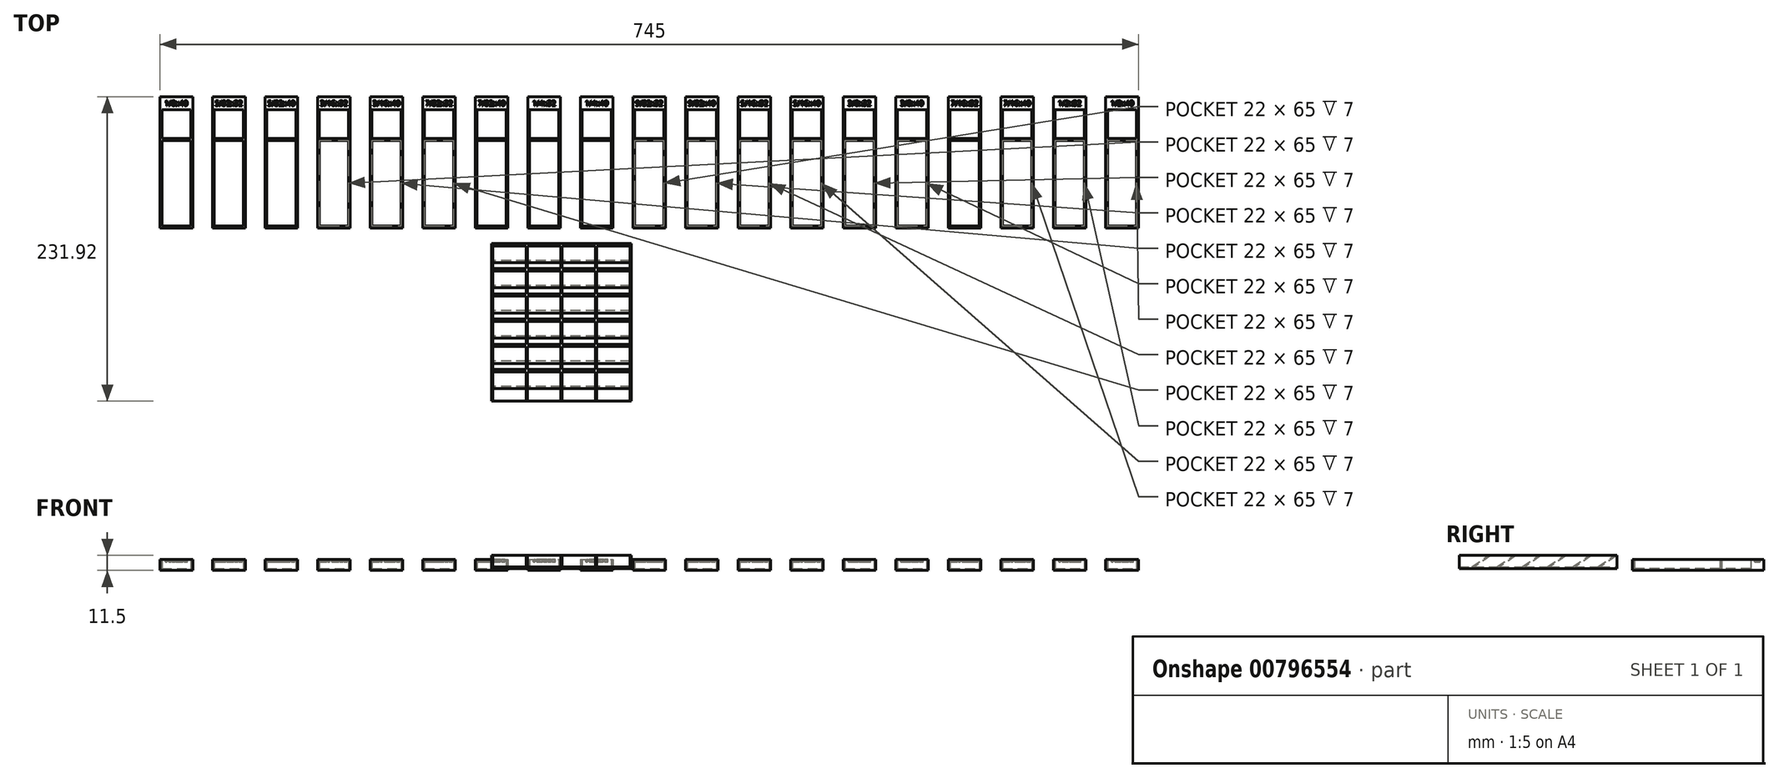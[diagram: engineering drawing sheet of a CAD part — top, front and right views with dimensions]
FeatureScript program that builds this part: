
annotation { "Feature Type Name" : "Feature", "Feature Type Description" : "" }
export const myFeature = defineFeature(function(context is Context, id is Id, definition is map)
    precondition{}
    {
        {
            var Q0;
            Q0=qCreatedBy(makeId("Top.planeOp"),FACE);
            var sketch = newSketch(context, id + "F0", { "sketchPlane" : qUnion([Q0])});
            skLineSegment(sketch, "E0.bottom", {"start": v(30.55, 66.22) * mm, "end": v(55.55, 66.22) * mm});
            skLineSegment(sketch, "E0.top", {"start": v(30.55, -33.78) * mm, "end": v(55.55, -33.78) * mm});
            skLineSegment(sketch, "E0.left", {"start": v(30.55, 66.22) * mm, "end": v(30.55, -33.78) * mm});
            skLineSegment(sketch, "E0.right", {"start": v(55.55, 66.22) * mm, "end": v(55.55, -33.78) * mm});
            skLineSegment(sketch, "E1.bottom", {"start": v(32.05, 56.22) * mm, "end": v(54.05, 56.22) * mm});
            skLineSegment(sketch, "E1.top", {"start": v(32.05, 34.22) * mm, "end": v(54.05, 34.22) * mm});
            skLineSegment(sketch, "E1.left", {"start": v(32.05, 56.22) * mm, "end": v(32.05, 34.22) * mm});
            skLineSegment(sketch, "E1.right", {"start": v(54.05, 56.22) * mm, "end": v(54.05, 34.22) * mm});
            skLineSegment(sketch, "E2.bottom", {"start": v(42.3, 32.72) * mm, "end": v(43.8, 32.72) * mm});
            skLineSegment(sketch, "E2.top", {"start": v(42.3, -32.28) * mm, "end": v(43.8, -32.28) * mm});
            skLineSegment(sketch, "E2.left", {"start": v(42.3, 32.72) * mm, "end": v(42.3, -32.28) * mm});
            skLineSegment(sketch, "E2.right", {"start": v(43.8, 32.72) * mm, "end": v(43.8, -32.28) * mm});
            skLineSegment(sketch, "E3.bottom", {"start": v(32.05, 32.72) * mm, "end": v(54.05, 32.72) * mm});
            skLineSegment(sketch, "E3.top", {"start": v(32.05, -32.28) * mm, "end": v(54.05, -32.28) * mm});
            skLineSegment(sketch, "E3.left", {"start": v(32.05, 32.72) * mm, "end": v(32.05, -32.28) * mm});
            skLineSegment(sketch, "E3.right", {"start": v(54.05, 32.72) * mm, "end": v(54.05, -32.28) * mm});
            skLineSegment(sketch, "E4", {"start": v(43.05, 66.22) * mm, "end": v(43.05, -33.78) * mm, "construction": true});
            skLineSegment(sketch, "E5.1.0.0", {"start": v(72.05, 34.22) * mm, "end": v(94.05, 34.22) * mm});
            skLineSegment(sketch, "E5.1.0.1", {"start": v(72.05, 56.22) * mm, "end": v(72.05, 34.22) * mm});
            skLineSegment(sketch, "E5.1.0.2", {"start": v(72.05, 32.72) * mm, "end": v(72.05, -32.28) * mm});
            skLineSegment(sketch, "E5.1.0.3", {"start": v(70.55, 66.22) * mm, "end": v(70.55, -33.78) * mm});
            skLineSegment(sketch, "E5.1.0.4", {"start": v(72.05, -32.28) * mm, "end": v(94.05, -32.28) * mm});
            skLineSegment(sketch, "E5.1.0.5", {"start": v(94.05, 32.72) * mm, "end": v(94.05, -32.28) * mm});
            skLineSegment(sketch, "E5.1.0.6", {"start": v(82.3, 32.72) * mm, "end": v(82.3, -32.28) * mm});
            skLineSegment(sketch, "E5.1.0.7", {"start": v(95.55, 66.22) * mm, "end": v(95.55, -33.78) * mm});
            skLineSegment(sketch, "E5.1.0.8", {"start": v(94.05, 56.22) * mm, "end": v(94.05, 34.22) * mm});
            skLineSegment(sketch, "E5.1.0.9", {"start": v(83.05, 66.22) * mm, "end": v(83.05, -33.78) * mm, "construction": true});
            skLineSegment(sketch, "E5.1.0.10", {"start": v(72.05, 32.72) * mm, "end": v(94.05, 32.72) * mm});
            skLineSegment(sketch, "E5.1.0.11", {"start": v(70.55, 66.22) * mm, "end": v(95.55, 66.22) * mm});
            skLineSegment(sketch, "E5.1.0.12", {"start": v(70.55, -33.78) * mm, "end": v(95.55, -33.78) * mm});
            skLineSegment(sketch, "E5.1.0.13", {"start": v(72.05, 56.22) * mm, "end": v(94.05, 56.22) * mm});
            skLineSegment(sketch, "E5.1.0.14", {"start": v(83.8, 32.72) * mm, "end": v(83.8, -32.28) * mm});
            skLineSegment(sketch, "E5.1.0.15", {"start": v(82.3, -32.28) * mm, "end": v(83.8, -32.28) * mm});
            skLineSegment(sketch, "E5.1.0.16", {"start": v(82.3, 32.72) * mm, "end": v(83.8, 32.72) * mm});
            skLineSegment(sketch, "E5.2.0.0", {"start": v(112.05, 34.22) * mm, "end": v(134.05, 34.22) * mm});
            skLineSegment(sketch, "E5.2.0.1", {"start": v(112.05, 56.22) * mm, "end": v(112.05, 34.22) * mm});
            skLineSegment(sketch, "E5.2.0.2", {"start": v(112.05, 32.72) * mm, "end": v(112.05, -32.28) * mm});
            skLineSegment(sketch, "E5.2.0.3", {"start": v(110.55, 66.22) * mm, "end": v(110.55, -33.78) * mm});
            skLineSegment(sketch, "E5.2.0.4", {"start": v(112.05, -32.28) * mm, "end": v(134.05, -32.28) * mm});
            skLineSegment(sketch, "E5.2.0.5", {"start": v(134.05, 32.72) * mm, "end": v(134.05, -32.28) * mm});
            skLineSegment(sketch, "E5.2.0.6", {"start": v(122.3, 32.72) * mm, "end": v(122.3, -32.28) * mm});
            skLineSegment(sketch, "E5.2.0.7", {"start": v(135.55, 66.22) * mm, "end": v(135.55, -33.78) * mm});
            skLineSegment(sketch, "E5.2.0.8", {"start": v(134.05, 56.22) * mm, "end": v(134.05, 34.22) * mm});
            skLineSegment(sketch, "E5.2.0.9", {"start": v(123.05, 66.22) * mm, "end": v(123.05, -33.78) * mm, "construction": true});
            skLineSegment(sketch, "E5.2.0.10", {"start": v(112.05, 32.72) * mm, "end": v(134.05, 32.72) * mm});
            skLineSegment(sketch, "E5.2.0.11", {"start": v(110.55, 66.22) * mm, "end": v(135.55, 66.22) * mm});
            skLineSegment(sketch, "E5.2.0.12", {"start": v(110.55, -33.78) * mm, "end": v(135.55, -33.78) * mm});
            skLineSegment(sketch, "E5.2.0.13", {"start": v(112.05, 56.22) * mm, "end": v(134.05, 56.22) * mm});
            skLineSegment(sketch, "E5.2.0.14", {"start": v(123.8, 32.72) * mm, "end": v(123.8, -32.28) * mm});
            skLineSegment(sketch, "E5.2.0.15", {"start": v(122.3, -32.28) * mm, "end": v(123.8, -32.28) * mm});
            skLineSegment(sketch, "E5.2.0.16", {"start": v(122.3, 32.72) * mm, "end": v(123.8, 32.72) * mm});
            skLineSegment(sketch, "E5.direction1", {"start": v(30.55, -33.78) * mm, "end": v(70.55, -33.78) * mm, "construction": true});
            skLineSegment(sketch, "E6.0.3.0", {"start": v(152.05, 34.22) * mm, "end": v(174.05, 34.22) * mm});
            skLineSegment(sketch, "E6.3.3.0", {"start": v(152.05, 56.22) * mm, "end": v(152.05, 34.22) * mm});
            skLineSegment(sketch, "E6.6.3.0", {"start": v(152.05, 32.72) * mm, "end": v(152.05, -32.28) * mm});
            skLineSegment(sketch, "E6.9.3.0", {"start": v(150.55, 66.22) * mm, "end": v(150.55, -33.78) * mm});
            skLineSegment(sketch, "E6.12.3.0", {"start": v(152.05, -32.28) * mm, "end": v(174.05, -32.28) * mm});
            skLineSegment(sketch, "E6.15.3.0", {"start": v(174.05, 32.72) * mm, "end": v(174.05, -32.28) * mm});
            skLineSegment(sketch, "E6.18.3.0", {"start": v(162.3, 32.72) * mm, "end": v(162.3, -32.28) * mm});
            skLineSegment(sketch, "E6.21.3.0", {"start": v(175.55, 66.22) * mm, "end": v(175.55, -33.78) * mm});
            skLineSegment(sketch, "E6.24.3.0", {"start": v(174.05, 56.22) * mm, "end": v(174.05, 34.22) * mm});
            skLineSegment(sketch, "E6.27.3.0", {"start": v(163.05, 66.22) * mm, "end": v(163.05, -33.78) * mm, "construction": true});
            skLineSegment(sketch, "E6.30.3.0", {"start": v(152.05, 32.72) * mm, "end": v(174.05, 32.72) * mm});
            skLineSegment(sketch, "E6.33.3.0", {"start": v(150.55, 66.22) * mm, "end": v(175.55, 66.22) * mm});
            skLineSegment(sketch, "E6.36.3.0", {"start": v(150.55, -33.78) * mm, "end": v(175.55, -33.78) * mm});
            skLineSegment(sketch, "E6.39.3.0", {"start": v(152.05, 56.22) * mm, "end": v(174.05, 56.22) * mm});
            skLineSegment(sketch, "E6.42.3.0", {"start": v(163.8, 32.72) * mm, "end": v(163.8, -32.28) * mm});
            skLineSegment(sketch, "E6.45.3.0", {"start": v(162.3, -32.28) * mm, "end": v(163.8, -32.28) * mm});
            skLineSegment(sketch, "E6.48.3.0", {"start": v(162.3, 32.72) * mm, "end": v(163.8, 32.72) * mm});
            skLineSegment(sketch, "E6.0.4.0", {"start": v(192.05, 34.22) * mm, "end": v(214.05, 34.22) * mm});
            skLineSegment(sketch, "E6.3.4.0", {"start": v(192.05, 56.22) * mm, "end": v(192.05, 34.22) * mm});
            skLineSegment(sketch, "E6.6.4.0", {"start": v(192.05, 32.72) * mm, "end": v(192.05, -32.28) * mm});
            skLineSegment(sketch, "E6.9.4.0", {"start": v(190.55, 66.22) * mm, "end": v(190.55, -33.78) * mm});
            skLineSegment(sketch, "E6.12.4.0", {"start": v(192.05, -32.28) * mm, "end": v(214.05, -32.28) * mm});
            skLineSegment(sketch, "E6.15.4.0", {"start": v(214.05, 32.72) * mm, "end": v(214.05, -32.28) * mm});
            skLineSegment(sketch, "E6.18.4.0", {"start": v(202.3, 32.72) * mm, "end": v(202.3, -32.28) * mm});
            skLineSegment(sketch, "E6.21.4.0", {"start": v(215.55, 66.22) * mm, "end": v(215.55, -33.78) * mm});
            skLineSegment(sketch, "E6.24.4.0", {"start": v(214.05, 56.22) * mm, "end": v(214.05, 34.22) * mm});
            skLineSegment(sketch, "E6.27.4.0", {"start": v(203.05, 66.22) * mm, "end": v(203.05, -33.78) * mm, "construction": true});
            skLineSegment(sketch, "E6.30.4.0", {"start": v(192.05, 32.72) * mm, "end": v(214.05, 32.72) * mm});
            skLineSegment(sketch, "E6.33.4.0", {"start": v(190.55, 66.22) * mm, "end": v(215.55, 66.22) * mm});
            skLineSegment(sketch, "E6.36.4.0", {"start": v(190.55, -33.78) * mm, "end": v(215.55, -33.78) * mm});
            skLineSegment(sketch, "E6.39.4.0", {"start": v(192.05, 56.22) * mm, "end": v(214.05, 56.22) * mm});
            skLineSegment(sketch, "E6.42.4.0", {"start": v(203.8, 32.72) * mm, "end": v(203.8, -32.28) * mm});
            skLineSegment(sketch, "E6.45.4.0", {"start": v(202.3, -32.28) * mm, "end": v(203.8, -32.28) * mm});
            skLineSegment(sketch, "E6.48.4.0", {"start": v(202.3, 32.72) * mm, "end": v(203.8, 32.72) * mm});
            skLineSegment(sketch, "E6.0.5.0", {"start": v(232.05, 34.22) * mm, "end": v(254.05, 34.22) * mm});
            skLineSegment(sketch, "E6.3.5.0", {"start": v(232.05, 56.22) * mm, "end": v(232.05, 34.22) * mm});
            skLineSegment(sketch, "E6.6.5.0", {"start": v(232.05, 32.72) * mm, "end": v(232.05, -32.28) * mm});
            skLineSegment(sketch, "E6.9.5.0", {"start": v(230.55, 66.22) * mm, "end": v(230.55, -33.78) * mm});
            skLineSegment(sketch, "E6.12.5.0", {"start": v(232.05, -32.28) * mm, "end": v(254.05, -32.28) * mm});
            skLineSegment(sketch, "E6.15.5.0", {"start": v(254.05, 32.72) * mm, "end": v(254.05, -32.28) * mm});
            skLineSegment(sketch, "E6.18.5.0", {"start": v(242.3, 32.72) * mm, "end": v(242.3, -32.28) * mm});
            skLineSegment(sketch, "E6.21.5.0", {"start": v(255.55, 66.22) * mm, "end": v(255.55, -33.78) * mm});
            skLineSegment(sketch, "E6.24.5.0", {"start": v(254.05, 56.22) * mm, "end": v(254.05, 34.22) * mm});
            skLineSegment(sketch, "E6.27.5.0", {"start": v(243.05, 66.22) * mm, "end": v(243.05, -33.78) * mm, "construction": true});
            skLineSegment(sketch, "E6.30.5.0", {"start": v(232.05, 32.72) * mm, "end": v(254.05, 32.72) * mm});
            skLineSegment(sketch, "E6.33.5.0", {"start": v(230.55, 66.22) * mm, "end": v(255.55, 66.22) * mm});
            skLineSegment(sketch, "E6.36.5.0", {"start": v(230.55, -33.78) * mm, "end": v(255.55, -33.78) * mm});
            skLineSegment(sketch, "E6.39.5.0", {"start": v(232.05, 56.22) * mm, "end": v(254.05, 56.22) * mm});
            skLineSegment(sketch, "E6.42.5.0", {"start": v(243.8, 32.72) * mm, "end": v(243.8, -32.28) * mm});
            skLineSegment(sketch, "E6.45.5.0", {"start": v(242.3, -32.28) * mm, "end": v(243.8, -32.28) * mm});
            skLineSegment(sketch, "E6.48.5.0", {"start": v(242.3, 32.72) * mm, "end": v(243.8, 32.72) * mm});
            skLineSegment(sketch, "E6.0.6.0", {"start": v(272.05, 34.22) * mm, "end": v(294.05, 34.22) * mm});
            skLineSegment(sketch, "E6.3.6.0", {"start": v(272.05, 56.22) * mm, "end": v(272.05, 34.22) * mm});
            skLineSegment(sketch, "E6.6.6.0", {"start": v(272.05, 32.72) * mm, "end": v(272.05, -32.28) * mm});
            skLineSegment(sketch, "E6.9.6.0", {"start": v(270.55, 66.22) * mm, "end": v(270.55, -33.78) * mm});
            skLineSegment(sketch, "E6.12.6.0", {"start": v(272.05, -32.28) * mm, "end": v(294.05, -32.28) * mm});
            skLineSegment(sketch, "E6.15.6.0", {"start": v(294.05, 32.72) * mm, "end": v(294.05, -32.28) * mm});
            skLineSegment(sketch, "E6.18.6.0", {"start": v(282.3, 32.72) * mm, "end": v(282.3, -32.28) * mm});
            skLineSegment(sketch, "E6.21.6.0", {"start": v(295.55, 66.22) * mm, "end": v(295.55, -33.78) * mm});
            skLineSegment(sketch, "E6.24.6.0", {"start": v(294.05, 56.22) * mm, "end": v(294.05, 34.22) * mm});
            skLineSegment(sketch, "E6.27.6.0", {"start": v(283.05, 66.22) * mm, "end": v(283.05, -33.78) * mm, "construction": true});
            skLineSegment(sketch, "E6.30.6.0", {"start": v(272.05, 32.72) * mm, "end": v(294.05, 32.72) * mm});
            skLineSegment(sketch, "E6.33.6.0", {"start": v(270.55, 66.22) * mm, "end": v(295.55, 66.22) * mm});
            skLineSegment(sketch, "E6.36.6.0", {"start": v(270.55, -33.78) * mm, "end": v(295.55, -33.78) * mm});
            skLineSegment(sketch, "E6.39.6.0", {"start": v(272.05, 56.22) * mm, "end": v(294.05, 56.22) * mm});
            skLineSegment(sketch, "E6.42.6.0", {"start": v(283.8, 32.72) * mm, "end": v(283.8, -32.28) * mm});
            skLineSegment(sketch, "E6.45.6.0", {"start": v(282.3, -32.28) * mm, "end": v(283.8, -32.28) * mm});
            skLineSegment(sketch, "E6.48.6.0", {"start": v(282.3, 32.72) * mm, "end": v(283.8, 32.72) * mm});
            skLineSegment(sketch, "E6.0.7.0", {"start": v(312.05, 34.22) * mm, "end": v(334.05, 34.22) * mm});
            skLineSegment(sketch, "E6.3.7.0", {"start": v(312.05, 56.22) * mm, "end": v(312.05, 34.22) * mm});
            skLineSegment(sketch, "E6.6.7.0", {"start": v(312.05, 32.72) * mm, "end": v(312.05, -32.28) * mm});
            skLineSegment(sketch, "E6.9.7.0", {"start": v(310.55, 66.22) * mm, "end": v(310.55, -33.78) * mm});
            skLineSegment(sketch, "E6.12.7.0", {"start": v(312.05, -32.28) * mm, "end": v(334.05, -32.28) * mm});
            skLineSegment(sketch, "E6.15.7.0", {"start": v(334.05, 32.72) * mm, "end": v(334.05, -32.28) * mm});
            skLineSegment(sketch, "E6.18.7.0", {"start": v(322.3, 32.72) * mm, "end": v(322.3, -32.28) * mm});
            skLineSegment(sketch, "E6.21.7.0", {"start": v(335.55, 66.22) * mm, "end": v(335.55, -33.78) * mm});
            skLineSegment(sketch, "E6.24.7.0", {"start": v(334.05, 56.22) * mm, "end": v(334.05, 34.22) * mm});
            skLineSegment(sketch, "E6.27.7.0", {"start": v(323.05, 66.22) * mm, "end": v(323.05, -33.78) * mm, "construction": true});
            skLineSegment(sketch, "E6.30.7.0", {"start": v(312.05, 32.72) * mm, "end": v(334.05, 32.72) * mm});
            skLineSegment(sketch, "E6.33.7.0", {"start": v(310.55, 66.22) * mm, "end": v(335.55, 66.22) * mm});
            skLineSegment(sketch, "E6.36.7.0", {"start": v(310.55, -33.78) * mm, "end": v(335.55, -33.78) * mm});
            skLineSegment(sketch, "E6.39.7.0", {"start": v(312.05, 56.22) * mm, "end": v(334.05, 56.22) * mm});
            skLineSegment(sketch, "E6.42.7.0", {"start": v(323.8, 32.72) * mm, "end": v(323.8, -32.28) * mm});
            skLineSegment(sketch, "E6.45.7.0", {"start": v(322.3, -32.28) * mm, "end": v(323.8, -32.28) * mm});
            skLineSegment(sketch, "E6.48.7.0", {"start": v(322.3, 32.72) * mm, "end": v(323.8, 32.72) * mm});
            skLineSegment(sketch, "E6.0.8.0", {"start": v(352.05, 34.22) * mm, "end": v(374.05, 34.22) * mm});
            skLineSegment(sketch, "E6.3.8.0", {"start": v(352.05, 56.22) * mm, "end": v(352.05, 34.22) * mm});
            skLineSegment(sketch, "E6.6.8.0", {"start": v(352.05, 32.72) * mm, "end": v(352.05, -32.28) * mm});
            skLineSegment(sketch, "E6.9.8.0", {"start": v(350.55, 66.22) * mm, "end": v(350.55, -33.78) * mm});
            skLineSegment(sketch, "E6.12.8.0", {"start": v(352.05, -32.28) * mm, "end": v(374.05, -32.28) * mm});
            skLineSegment(sketch, "E6.15.8.0", {"start": v(374.05, 32.72) * mm, "end": v(374.05, -32.28) * mm});
            skLineSegment(sketch, "E6.18.8.0", {"start": v(362.3, 32.72) * mm, "end": v(362.3, -32.28) * mm});
            skLineSegment(sketch, "E6.21.8.0", {"start": v(375.55, 66.22) * mm, "end": v(375.55, -33.78) * mm});
            skLineSegment(sketch, "E6.24.8.0", {"start": v(374.05, 56.22) * mm, "end": v(374.05, 34.22) * mm});
            skLineSegment(sketch, "E6.27.8.0", {"start": v(363.05, 66.22) * mm, "end": v(363.05, -33.78) * mm, "construction": true});
            skLineSegment(sketch, "E6.30.8.0", {"start": v(352.05, 32.72) * mm, "end": v(374.05, 32.72) * mm});
            skLineSegment(sketch, "E6.33.8.0", {"start": v(350.55, 66.22) * mm, "end": v(375.55, 66.22) * mm});
            skLineSegment(sketch, "E6.36.8.0", {"start": v(350.55, -33.78) * mm, "end": v(375.55, -33.78) * mm});
            skLineSegment(sketch, "E6.39.8.0", {"start": v(352.05, 56.22) * mm, "end": v(374.05, 56.22) * mm});
            skLineSegment(sketch, "E6.42.8.0", {"start": v(363.8, 32.72) * mm, "end": v(363.8, -32.28) * mm});
            skLineSegment(sketch, "E6.45.8.0", {"start": v(362.3, -32.28) * mm, "end": v(363.8, -32.28) * mm});
            skLineSegment(sketch, "E6.48.8.0", {"start": v(362.3, 32.72) * mm, "end": v(363.8, 32.72) * mm});
            skLineSegment(sketch, "E6.0.9.0", {"start": v(392.05, 34.22) * mm, "end": v(414.05, 34.22) * mm});
            skLineSegment(sketch, "E6.3.9.0", {"start": v(392.05, 56.22) * mm, "end": v(392.05, 34.22) * mm});
            skLineSegment(sketch, "E6.6.9.0", {"start": v(392.05, 32.72) * mm, "end": v(392.05, -32.28) * mm});
            skLineSegment(sketch, "E6.9.9.0", {"start": v(390.55, 66.22) * mm, "end": v(390.55, -33.78) * mm});
            skLineSegment(sketch, "E6.12.9.0", {"start": v(392.05, -32.28) * mm, "end": v(414.05, -32.28) * mm});
            skLineSegment(sketch, "E6.15.9.0", {"start": v(414.05, 32.72) * mm, "end": v(414.05, -32.28) * mm});
            skLineSegment(sketch, "E6.18.9.0", {"start": v(402.3, 32.72) * mm, "end": v(402.3, -32.28) * mm});
            skLineSegment(sketch, "E6.21.9.0", {"start": v(415.55, 66.22) * mm, "end": v(415.55, -33.78) * mm});
            skLineSegment(sketch, "E6.24.9.0", {"start": v(414.05, 56.22) * mm, "end": v(414.05, 34.22) * mm});
            skLineSegment(sketch, "E6.27.9.0", {"start": v(403.05, 66.22) * mm, "end": v(403.05, -33.78) * mm, "construction": true});
            skLineSegment(sketch, "E6.30.9.0", {"start": v(392.05, 32.72) * mm, "end": v(414.05, 32.72) * mm});
            skLineSegment(sketch, "E6.33.9.0", {"start": v(390.55, 66.22) * mm, "end": v(415.55, 66.22) * mm});
            skLineSegment(sketch, "E6.36.9.0", {"start": v(390.55, -33.78) * mm, "end": v(415.55, -33.78) * mm});
            skLineSegment(sketch, "E6.39.9.0", {"start": v(392.05, 56.22) * mm, "end": v(414.05, 56.22) * mm});
            skLineSegment(sketch, "E6.42.9.0", {"start": v(403.8, 32.72) * mm, "end": v(403.8, -32.28) * mm});
            skLineSegment(sketch, "E6.45.9.0", {"start": v(402.3, -32.28) * mm, "end": v(403.8, -32.28) * mm});
            skLineSegment(sketch, "E6.48.9.0", {"start": v(402.3, 32.72) * mm, "end": v(403.8, 32.72) * mm});
            skLineSegment(sketch, "E6.0.10.0", {"start": v(432.05, 34.22) * mm, "end": v(454.05, 34.22) * mm});
            skLineSegment(sketch, "E6.3.10.0", {"start": v(432.05, 56.22) * mm, "end": v(432.05, 34.22) * mm});
            skLineSegment(sketch, "E6.6.10.0", {"start": v(432.05, 32.72) * mm, "end": v(432.05, -32.28) * mm});
            skLineSegment(sketch, "E6.9.10.0", {"start": v(430.55, 66.22) * mm, "end": v(430.55, -33.78) * mm});
            skLineSegment(sketch, "E6.12.10.0", {"start": v(432.05, -32.28) * mm, "end": v(454.05, -32.28) * mm});
            skLineSegment(sketch, "E6.15.10.0", {"start": v(454.05, 32.72) * mm, "end": v(454.05, -32.28) * mm});
            skLineSegment(sketch, "E6.18.10.0", {"start": v(442.3, 32.72) * mm, "end": v(442.3, -32.28) * mm});
            skLineSegment(sketch, "E6.21.10.0", {"start": v(455.55, 66.22) * mm, "end": v(455.55, -33.78) * mm});
            skLineSegment(sketch, "E6.24.10.0", {"start": v(454.05, 56.22) * mm, "end": v(454.05, 34.22) * mm});
            skLineSegment(sketch, "E6.27.10.0", {"start": v(443.05, 66.22) * mm, "end": v(443.05, -33.78) * mm, "construction": true});
            skLineSegment(sketch, "E6.30.10.0", {"start": v(432.05, 32.72) * mm, "end": v(454.05, 32.72) * mm});
            skLineSegment(sketch, "E6.33.10.0", {"start": v(430.55, 66.22) * mm, "end": v(455.55, 66.22) * mm});
            skLineSegment(sketch, "E6.36.10.0", {"start": v(430.55, -33.78) * mm, "end": v(455.55, -33.78) * mm});
            skLineSegment(sketch, "E6.39.10.0", {"start": v(432.05, 56.22) * mm, "end": v(454.05, 56.22) * mm});
            skLineSegment(sketch, "E6.42.10.0", {"start": v(443.8, 32.72) * mm, "end": v(443.8, -32.28) * mm});
            skLineSegment(sketch, "E6.45.10.0", {"start": v(442.3, -32.28) * mm, "end": v(443.8, -32.28) * mm});
            skLineSegment(sketch, "E6.48.10.0", {"start": v(442.3, 32.72) * mm, "end": v(443.8, 32.72) * mm});
            skLineSegment(sketch, "E6.0.11.0", {"start": v(472.05, 34.22) * mm, "end": v(494.05, 34.22) * mm});
            skLineSegment(sketch, "E6.3.11.0", {"start": v(472.05, 56.22) * mm, "end": v(472.05, 34.22) * mm});
            skLineSegment(sketch, "E6.6.11.0", {"start": v(472.05, 32.72) * mm, "end": v(472.05, -32.28) * mm});
            skLineSegment(sketch, "E6.9.11.0", {"start": v(470.55, 66.22) * mm, "end": v(470.55, -33.78) * mm});
            skLineSegment(sketch, "E6.12.11.0", {"start": v(472.05, -32.28) * mm, "end": v(494.05, -32.28) * mm});
            skLineSegment(sketch, "E6.15.11.0", {"start": v(494.05, 32.72) * mm, "end": v(494.05, -32.28) * mm});
            skLineSegment(sketch, "E6.18.11.0", {"start": v(482.3, 32.72) * mm, "end": v(482.3, -32.28) * mm});
            skLineSegment(sketch, "E6.21.11.0", {"start": v(495.55, 66.22) * mm, "end": v(495.55, -33.78) * mm});
            skLineSegment(sketch, "E6.24.11.0", {"start": v(494.05, 56.22) * mm, "end": v(494.05, 34.22) * mm});
            skLineSegment(sketch, "E6.27.11.0", {"start": v(483.05, 66.22) * mm, "end": v(483.05, -33.78) * mm, "construction": true});
            skLineSegment(sketch, "E6.30.11.0", {"start": v(472.05, 32.72) * mm, "end": v(494.05, 32.72) * mm});
            skLineSegment(sketch, "E6.33.11.0", {"start": v(470.55, 66.22) * mm, "end": v(495.55, 66.22) * mm});
            skLineSegment(sketch, "E6.36.11.0", {"start": v(470.55, -33.78) * mm, "end": v(495.55, -33.78) * mm});
            skLineSegment(sketch, "E6.39.11.0", {"start": v(472.05, 56.22) * mm, "end": v(494.05, 56.22) * mm});
            skLineSegment(sketch, "E6.42.11.0", {"start": v(483.8, 32.72) * mm, "end": v(483.8, -32.28) * mm});
            skLineSegment(sketch, "E6.45.11.0", {"start": v(482.3, -32.28) * mm, "end": v(483.8, -32.28) * mm});
            skLineSegment(sketch, "E6.48.11.0", {"start": v(482.3, 32.72) * mm, "end": v(483.8, 32.72) * mm});
            skLineSegment(sketch, "E7.0.12.0", {"start": v(512.05, 34.22) * mm, "end": v(534.05, 34.22) * mm});
            skLineSegment(sketch, "E7.3.12.0", {"start": v(512.05, 56.22) * mm, "end": v(512.05, 34.22) * mm});
            skLineSegment(sketch, "E7.6.12.0", {"start": v(512.05, 32.72) * mm, "end": v(512.05, -32.28) * mm});
            skLineSegment(sketch, "E7.9.12.0", {"start": v(510.55, 66.22) * mm, "end": v(510.55, -33.78) * mm});
            skLineSegment(sketch, "E7.12.12.0", {"start": v(512.05, -32.28) * mm, "end": v(534.05, -32.28) * mm});
            skLineSegment(sketch, "E7.15.12.0", {"start": v(534.05, 32.72) * mm, "end": v(534.05, -32.28) * mm});
            skLineSegment(sketch, "E7.18.12.0", {"start": v(522.3, 32.72) * mm, "end": v(522.3, -32.28) * mm});
            skLineSegment(sketch, "E7.21.12.0", {"start": v(535.55, 66.22) * mm, "end": v(535.55, -33.78) * mm});
            skLineSegment(sketch, "E7.24.12.0", {"start": v(534.05, 56.22) * mm, "end": v(534.05, 34.22) * mm});
            skLineSegment(sketch, "E7.27.12.0", {"start": v(523.05, 66.22) * mm, "end": v(523.05, -33.78) * mm, "construction": true});
            skLineSegment(sketch, "E7.30.12.0", {"start": v(512.05, 32.72) * mm, "end": v(534.05, 32.72) * mm});
            skLineSegment(sketch, "E7.33.12.0", {"start": v(510.55, 66.22) * mm, "end": v(535.55, 66.22) * mm});
            skLineSegment(sketch, "E7.36.12.0", {"start": v(510.55, -33.78) * mm, "end": v(535.55, -33.78) * mm});
            skLineSegment(sketch, "E7.39.12.0", {"start": v(512.05, 56.22) * mm, "end": v(534.05, 56.22) * mm});
            skLineSegment(sketch, "E7.42.12.0", {"start": v(523.8, 32.72) * mm, "end": v(523.8, -32.28) * mm});
            skLineSegment(sketch, "E7.45.12.0", {"start": v(522.3, -32.28) * mm, "end": v(523.8, -32.28) * mm});
            skLineSegment(sketch, "E7.48.12.0", {"start": v(522.3, 32.72) * mm, "end": v(523.8, 32.72) * mm});
            skLineSegment(sketch, "E8.0.13.0", {"start": v(552.05, 34.22) * mm, "end": v(574.05, 34.22) * mm});
            skLineSegment(sketch, "E8.3.13.0", {"start": v(552.05, 56.22) * mm, "end": v(552.05, 34.22) * mm});
            skLineSegment(sketch, "E8.6.13.0", {"start": v(552.05, 32.72) * mm, "end": v(552.05, -32.28) * mm});
            skLineSegment(sketch, "E8.9.13.0", {"start": v(550.55, 66.22) * mm, "end": v(550.55, -33.78) * mm});
            skLineSegment(sketch, "E8.12.13.0", {"start": v(552.05, -32.28) * mm, "end": v(574.05, -32.28) * mm});
            skLineSegment(sketch, "E8.15.13.0", {"start": v(574.05, 32.72) * mm, "end": v(574.05, -32.28) * mm});
            skLineSegment(sketch, "E8.18.13.0", {"start": v(562.3, 32.72) * mm, "end": v(562.3, -32.28) * mm});
            skLineSegment(sketch, "E8.21.13.0", {"start": v(575.55, 66.22) * mm, "end": v(575.55, -33.78) * mm});
            skLineSegment(sketch, "E8.24.13.0", {"start": v(574.05, 56.22) * mm, "end": v(574.05, 34.22) * mm});
            skLineSegment(sketch, "E8.27.13.0", {"start": v(563.05, 66.22) * mm, "end": v(563.05, -33.78) * mm, "construction": true});
            skLineSegment(sketch, "E8.30.13.0", {"start": v(552.05, 32.72) * mm, "end": v(574.05, 32.72) * mm});
            skLineSegment(sketch, "E8.33.13.0", {"start": v(550.55, 66.22) * mm, "end": v(575.55, 66.22) * mm});
            skLineSegment(sketch, "E8.36.13.0", {"start": v(550.55, -33.78) * mm, "end": v(575.55, -33.78) * mm});
            skLineSegment(sketch, "E8.39.13.0", {"start": v(552.05, 56.22) * mm, "end": v(574.05, 56.22) * mm});
            skLineSegment(sketch, "E8.42.13.0", {"start": v(563.8, 32.72) * mm, "end": v(563.8, -32.28) * mm});
            skLineSegment(sketch, "E8.45.13.0", {"start": v(562.3, -32.28) * mm, "end": v(563.8, -32.28) * mm});
            skLineSegment(sketch, "E8.48.13.0", {"start": v(562.3, 32.72) * mm, "end": v(563.8, 32.72) * mm});
            skLineSegment(sketch, "E8.0.14.0", {"start": v(592.05, 34.22) * mm, "end": v(614.05, 34.22) * mm});
            skLineSegment(sketch, "E8.3.14.0", {"start": v(592.05, 56.22) * mm, "end": v(592.05, 34.22) * mm});
            skLineSegment(sketch, "E8.6.14.0", {"start": v(592.05, 32.72) * mm, "end": v(592.05, -32.28) * mm});
            skLineSegment(sketch, "E8.9.14.0", {"start": v(590.55, 66.22) * mm, "end": v(590.55, -33.78) * mm});
            skLineSegment(sketch, "E8.12.14.0", {"start": v(592.05, -32.28) * mm, "end": v(614.05, -32.28) * mm});
            skLineSegment(sketch, "E8.15.14.0", {"start": v(614.05, 32.72) * mm, "end": v(614.05, -32.28) * mm});
            skLineSegment(sketch, "E8.18.14.0", {"start": v(602.3, 32.72) * mm, "end": v(602.3, -32.28) * mm});
            skLineSegment(sketch, "E8.21.14.0", {"start": v(615.55, 66.22) * mm, "end": v(615.55, -33.78) * mm});
            skLineSegment(sketch, "E8.24.14.0", {"start": v(614.05, 56.22) * mm, "end": v(614.05, 34.22) * mm});
            skLineSegment(sketch, "E8.27.14.0", {"start": v(603.05, 66.22) * mm, "end": v(603.05, -33.78) * mm, "construction": true});
            skLineSegment(sketch, "E8.30.14.0", {"start": v(592.05, 32.72) * mm, "end": v(614.05, 32.72) * mm});
            skLineSegment(sketch, "E8.33.14.0", {"start": v(590.55, 66.22) * mm, "end": v(615.55, 66.22) * mm});
            skLineSegment(sketch, "E8.36.14.0", {"start": v(590.55, -33.78) * mm, "end": v(615.55, -33.78) * mm});
            skLineSegment(sketch, "E8.39.14.0", {"start": v(592.05, 56.22) * mm, "end": v(614.05, 56.22) * mm});
            skLineSegment(sketch, "E8.42.14.0", {"start": v(603.8, 32.72) * mm, "end": v(603.8, -32.28) * mm});
            skLineSegment(sketch, "E8.45.14.0", {"start": v(602.3, -32.28) * mm, "end": v(603.8, -32.28) * mm});
            skLineSegment(sketch, "E8.48.14.0", {"start": v(602.3, 32.72) * mm, "end": v(603.8, 32.72) * mm});
            skLineSegment(sketch, "E9.0.15.0", {"start": v(632.05, 34.22) * mm, "end": v(654.05, 34.22) * mm});
            skLineSegment(sketch, "E9.3.15.0", {"start": v(632.05, 56.22) * mm, "end": v(632.05, 34.22) * mm});
            skLineSegment(sketch, "E9.6.15.0", {"start": v(632.05, 32.72) * mm, "end": v(632.05, -32.28) * mm});
            skLineSegment(sketch, "E9.9.15.0", {"start": v(630.55, 66.22) * mm, "end": v(630.55, -33.78) * mm});
            skLineSegment(sketch, "E9.12.15.0", {"start": v(632.05, -32.28) * mm, "end": v(654.05, -32.28) * mm});
            skLineSegment(sketch, "E9.15.15.0", {"start": v(654.05, 32.72) * mm, "end": v(654.05, -32.28) * mm});
            skLineSegment(sketch, "E9.18.15.0", {"start": v(642.3, 32.72) * mm, "end": v(642.3, -32.28) * mm});
            skLineSegment(sketch, "E9.21.15.0", {"start": v(655.55, 66.22) * mm, "end": v(655.55, -33.78) * mm});
            skLineSegment(sketch, "E9.24.15.0", {"start": v(654.05, 56.22) * mm, "end": v(654.05, 34.22) * mm});
            skLineSegment(sketch, "E9.27.15.0", {"start": v(643.05, 66.22) * mm, "end": v(643.05, -33.78) * mm, "construction": true});
            skLineSegment(sketch, "E9.30.15.0", {"start": v(632.05, 32.72) * mm, "end": v(654.05, 32.72) * mm});
            skLineSegment(sketch, "E9.33.15.0", {"start": v(630.55, 66.22) * mm, "end": v(655.55, 66.22) * mm});
            skLineSegment(sketch, "E9.36.15.0", {"start": v(630.55, -33.78) * mm, "end": v(655.55, -33.78) * mm});
            skLineSegment(sketch, "E9.39.15.0", {"start": v(632.05, 56.22) * mm, "end": v(654.05, 56.22) * mm});
            skLineSegment(sketch, "E9.42.15.0", {"start": v(643.8, 32.72) * mm, "end": v(643.8, -32.28) * mm});
            skLineSegment(sketch, "E9.45.15.0", {"start": v(642.3, -32.28) * mm, "end": v(643.8, -32.28) * mm});
            skLineSegment(sketch, "E9.48.15.0", {"start": v(642.3, 32.72) * mm, "end": v(643.8, 32.72) * mm});
            skLineSegment(sketch, "E9.0.16.0", {"start": v(672.05, 34.22) * mm, "end": v(694.05, 34.22) * mm});
            skLineSegment(sketch, "E9.3.16.0", {"start": v(672.05, 56.22) * mm, "end": v(672.05, 34.22) * mm});
            skLineSegment(sketch, "E9.6.16.0", {"start": v(672.05, 32.72) * mm, "end": v(672.05, -32.28) * mm});
            skLineSegment(sketch, "E9.9.16.0", {"start": v(670.55, 66.22) * mm, "end": v(670.55, -33.78) * mm});
            skLineSegment(sketch, "E9.12.16.0", {"start": v(672.05, -32.28) * mm, "end": v(694.05, -32.28) * mm});
            skLineSegment(sketch, "E9.15.16.0", {"start": v(694.05, 32.72) * mm, "end": v(694.05, -32.28) * mm});
            skLineSegment(sketch, "E9.18.16.0", {"start": v(682.3, 32.72) * mm, "end": v(682.3, -32.28) * mm});
            skLineSegment(sketch, "E9.21.16.0", {"start": v(695.55, 66.22) * mm, "end": v(695.55, -33.78) * mm});
            skLineSegment(sketch, "E9.24.16.0", {"start": v(694.05, 56.22) * mm, "end": v(694.05, 34.22) * mm});
            skLineSegment(sketch, "E9.27.16.0", {"start": v(683.05, 66.22) * mm, "end": v(683.05, -33.78) * mm, "construction": true});
            skLineSegment(sketch, "E9.30.16.0", {"start": v(672.05, 32.72) * mm, "end": v(694.05, 32.72) * mm});
            skLineSegment(sketch, "E9.33.16.0", {"start": v(670.55, 66.22) * mm, "end": v(695.55, 66.22) * mm});
            skLineSegment(sketch, "E9.36.16.0", {"start": v(670.55, -33.78) * mm, "end": v(695.55, -33.78) * mm});
            skLineSegment(sketch, "E9.39.16.0", {"start": v(672.05, 56.22) * mm, "end": v(694.05, 56.22) * mm});
            skLineSegment(sketch, "E9.42.16.0", {"start": v(683.8, 32.72) * mm, "end": v(683.8, -32.28) * mm});
            skLineSegment(sketch, "E9.45.16.0", {"start": v(682.3, -32.28) * mm, "end": v(683.8, -32.28) * mm});
            skLineSegment(sketch, "E9.48.16.0", {"start": v(682.3, 32.72) * mm, "end": v(683.8, 32.72) * mm});
            skLineSegment(sketch, "E9.0.17.0", {"start": v(712.05, 34.22) * mm, "end": v(734.05, 34.22) * mm});
            skLineSegment(sketch, "E9.3.17.0", {"start": v(712.05, 56.22) * mm, "end": v(712.05, 34.22) * mm});
            skLineSegment(sketch, "E9.6.17.0", {"start": v(712.05, 32.72) * mm, "end": v(712.05, -32.28) * mm});
            skLineSegment(sketch, "E9.9.17.0", {"start": v(710.55, 66.22) * mm, "end": v(710.55, -33.78) * mm});
            skLineSegment(sketch, "E9.12.17.0", {"start": v(712.05, -32.28) * mm, "end": v(734.05, -32.28) * mm});
            skLineSegment(sketch, "E9.15.17.0", {"start": v(734.05, 32.72) * mm, "end": v(734.05, -32.28) * mm});
            skLineSegment(sketch, "E9.18.17.0", {"start": v(722.3, 32.72) * mm, "end": v(722.3, -32.28) * mm});
            skLineSegment(sketch, "E9.21.17.0", {"start": v(735.55, 66.22) * mm, "end": v(735.55, -33.78) * mm});
            skLineSegment(sketch, "E9.24.17.0", {"start": v(734.05, 56.22) * mm, "end": v(734.05, 34.22) * mm});
            skLineSegment(sketch, "E9.27.17.0", {"start": v(723.05, 66.22) * mm, "end": v(723.05, -33.78) * mm, "construction": true});
            skLineSegment(sketch, "E9.30.17.0", {"start": v(712.05, 32.72) * mm, "end": v(734.05, 32.72) * mm});
            skLineSegment(sketch, "E9.33.17.0", {"start": v(710.55, 66.22) * mm, "end": v(735.55, 66.22) * mm});
            skLineSegment(sketch, "E9.36.17.0", {"start": v(710.55, -33.78) * mm, "end": v(735.55, -33.78) * mm});
            skLineSegment(sketch, "E9.39.17.0", {"start": v(712.05, 56.22) * mm, "end": v(734.05, 56.22) * mm});
            skLineSegment(sketch, "E9.42.17.0", {"start": v(723.8, 32.72) * mm, "end": v(723.8, -32.28) * mm});
            skLineSegment(sketch, "E9.45.17.0", {"start": v(722.3, -32.28) * mm, "end": v(723.8, -32.28) * mm});
            skLineSegment(sketch, "E9.48.17.0", {"start": v(722.3, 32.72) * mm, "end": v(723.8, 32.72) * mm});
            skLineSegment(sketch, "E9.0.18.0", {"start": v(752.05, 34.22) * mm, "end": v(774.05, 34.22) * mm});
            skLineSegment(sketch, "E9.3.18.0", {"start": v(752.05, 56.22) * mm, "end": v(752.05, 34.22) * mm});
            skLineSegment(sketch, "E9.6.18.0", {"start": v(752.05, 32.72) * mm, "end": v(752.05, -32.28) * mm});
            skLineSegment(sketch, "E9.9.18.0", {"start": v(750.55, 66.22) * mm, "end": v(750.55, -33.78) * mm});
            skLineSegment(sketch, "E9.12.18.0", {"start": v(752.05, -32.28) * mm, "end": v(774.05, -32.28) * mm});
            skLineSegment(sketch, "E9.15.18.0", {"start": v(774.05, 32.72) * mm, "end": v(774.05, -32.28) * mm});
            skLineSegment(sketch, "E9.18.18.0", {"start": v(762.3, 32.72) * mm, "end": v(762.3, -32.28) * mm});
            skLineSegment(sketch, "E9.21.18.0", {"start": v(775.55, 66.22) * mm, "end": v(775.55, -33.78) * mm});
            skLineSegment(sketch, "E9.24.18.0", {"start": v(774.05, 56.22) * mm, "end": v(774.05, 34.22) * mm});
            skLineSegment(sketch, "E9.27.18.0", {"start": v(763.05, 66.22) * mm, "end": v(763.05, -33.78) * mm, "construction": true});
            skLineSegment(sketch, "E9.30.18.0", {"start": v(752.05, 32.72) * mm, "end": v(774.05, 32.72) * mm});
            skLineSegment(sketch, "E9.33.18.0", {"start": v(750.55, 66.22) * mm, "end": v(775.55, 66.22) * mm});
            skLineSegment(sketch, "E9.36.18.0", {"start": v(750.55, -33.78) * mm, "end": v(775.55, -33.78) * mm});
            skLineSegment(sketch, "E9.39.18.0", {"start": v(752.05, 56.22) * mm, "end": v(774.05, 56.22) * mm});
            skLineSegment(sketch, "E9.42.18.0", {"start": v(763.8, 32.72) * mm, "end": v(763.8, -32.28) * mm});
            skLineSegment(sketch, "E9.45.18.0", {"start": v(762.3, -32.28) * mm, "end": v(763.8, -32.28) * mm});
            skLineSegment(sketch, "E9.48.18.0", {"start": v(762.3, 32.72) * mm, "end": v(763.8, 32.72) * mm});
            skSolve(sketch);
        }
        {
            var Q0;
            Q0=qCreatedBy(makeId("Top.planeOp"),FACE);
            var sketch = newSketch(context, id + "F1", { "sketchPlane" : qUnion([Q0])});
            skLineSegment(sketch, "E10.bottom", {"start": v(30.55, 66.22) * mm, "end": v(55.55, 66.22) * mm});
            skLineSegment(sketch, "E10.top", {"start": v(30.55, -33.78) * mm, "end": v(55.55, -33.78) * mm});
            skLineSegment(sketch, "E10.left", {"start": v(30.55, 66.22) * mm, "end": v(30.55, -33.78) * mm});
            skLineSegment(sketch, "E10.right", {"start": v(55.55, 66.22) * mm, "end": v(55.55, -33.78) * mm});
            skLineSegment(sketch, "E11.1.0.0", {"start": v(70.55, 66.22) * mm, "end": v(95.55, 66.22) * mm});
            skLineSegment(sketch, "E11.1.0.1", {"start": v(70.55, 66.22) * mm, "end": v(70.55, -33.78) * mm});
            skLineSegment(sketch, "E11.1.0.2", {"start": v(70.55, -33.78) * mm, "end": v(95.55, -33.78) * mm});
            skLineSegment(sketch, "E11.1.0.3", {"start": v(95.55, 66.22) * mm, "end": v(95.55, -33.78) * mm});
            skLineSegment(sketch, "E11.2.0.0", {"start": v(110.55, 66.22) * mm, "end": v(135.55, 66.22) * mm});
            skLineSegment(sketch, "E11.2.0.1", {"start": v(110.55, 66.22) * mm, "end": v(110.55, -33.78) * mm});
            skLineSegment(sketch, "E11.2.0.2", {"start": v(110.55, -33.78) * mm, "end": v(135.55, -33.78) * mm});
            skLineSegment(sketch, "E11.2.0.3", {"start": v(135.55, 66.22) * mm, "end": v(135.55, -33.78) * mm});
            skLineSegment(sketch, "E11.direction1", {"start": v(30.55, 66.22) * mm, "end": v(70.55, 66.22) * mm, "construction": true});
            skLineSegment(sketch, "E12.0.3.0", {"start": v(150.55, 66.22) * mm, "end": v(175.55, 66.22) * mm});
            skLineSegment(sketch, "E12.3.3.0", {"start": v(150.55, 66.22) * mm, "end": v(150.55, -33.78) * mm});
            skLineSegment(sketch, "E12.6.3.0", {"start": v(150.55, -33.78) * mm, "end": v(175.55, -33.78) * mm});
            skLineSegment(sketch, "E12.9.3.0", {"start": v(175.55, 66.22) * mm, "end": v(175.55, -33.78) * mm});
            skLineSegment(sketch, "E12.0.4.0", {"start": v(190.55, 66.22) * mm, "end": v(215.55, 66.22) * mm});
            skLineSegment(sketch, "E12.3.4.0", {"start": v(190.55, 66.22) * mm, "end": v(190.55, -33.78) * mm});
            skLineSegment(sketch, "E12.6.4.0", {"start": v(190.55, -33.78) * mm, "end": v(215.55, -33.78) * mm});
            skLineSegment(sketch, "E12.9.4.0", {"start": v(215.55, 66.22) * mm, "end": v(215.55, -33.78) * mm});
            skLineSegment(sketch, "E12.0.5.0", {"start": v(230.55, 66.22) * mm, "end": v(255.55, 66.22) * mm});
            skLineSegment(sketch, "E12.3.5.0", {"start": v(230.55, 66.22) * mm, "end": v(230.55, -33.78) * mm});
            skLineSegment(sketch, "E12.6.5.0", {"start": v(230.55, -33.78) * mm, "end": v(255.55, -33.78) * mm});
            skLineSegment(sketch, "E12.9.5.0", {"start": v(255.55, 66.22) * mm, "end": v(255.55, -33.78) * mm});
            skLineSegment(sketch, "E12.0.6.0", {"start": v(270.55, 66.22) * mm, "end": v(295.55, 66.22) * mm});
            skLineSegment(sketch, "E12.3.6.0", {"start": v(270.55, 66.22) * mm, "end": v(270.55, -33.78) * mm});
            skLineSegment(sketch, "E12.6.6.0", {"start": v(270.55, -33.78) * mm, "end": v(295.55, -33.78) * mm});
            skLineSegment(sketch, "E12.9.6.0", {"start": v(295.55, 66.22) * mm, "end": v(295.55, -33.78) * mm});
            skLineSegment(sketch, "E12.0.7.0", {"start": v(310.55, 66.22) * mm, "end": v(335.55, 66.22) * mm});
            skLineSegment(sketch, "E12.3.7.0", {"start": v(310.55, 66.22) * mm, "end": v(310.55, -33.78) * mm});
            skLineSegment(sketch, "E12.6.7.0", {"start": v(310.55, -33.78) * mm, "end": v(335.55, -33.78) * mm});
            skLineSegment(sketch, "E12.9.7.0", {"start": v(335.55, 66.22) * mm, "end": v(335.55, -33.78) * mm});
            skLineSegment(sketch, "E12.0.8.0", {"start": v(350.55, 66.22) * mm, "end": v(375.55, 66.22) * mm});
            skLineSegment(sketch, "E12.3.8.0", {"start": v(350.55, 66.22) * mm, "end": v(350.55, -33.78) * mm});
            skLineSegment(sketch, "E12.6.8.0", {"start": v(350.55, -33.78) * mm, "end": v(375.55, -33.78) * mm});
            skLineSegment(sketch, "E12.9.8.0", {"start": v(375.55, 66.22) * mm, "end": v(375.55, -33.78) * mm});
            skLineSegment(sketch, "E12.0.9.0", {"start": v(390.55, 66.22) * mm, "end": v(415.55, 66.22) * mm});
            skLineSegment(sketch, "E12.3.9.0", {"start": v(390.55, 66.22) * mm, "end": v(390.55, -33.78) * mm});
            skLineSegment(sketch, "E12.6.9.0", {"start": v(390.55, -33.78) * mm, "end": v(415.55, -33.78) * mm});
            skLineSegment(sketch, "E12.9.9.0", {"start": v(415.55, 66.22) * mm, "end": v(415.55, -33.78) * mm});
            skLineSegment(sketch, "E12.0.10.0", {"start": v(430.55, 66.22) * mm, "end": v(455.55, 66.22) * mm});
            skLineSegment(sketch, "E12.3.10.0", {"start": v(430.55, 66.22) * mm, "end": v(430.55, -33.78) * mm});
            skLineSegment(sketch, "E12.6.10.0", {"start": v(430.55, -33.78) * mm, "end": v(455.55, -33.78) * mm});
            skLineSegment(sketch, "E12.9.10.0", {"start": v(455.55, 66.22) * mm, "end": v(455.55, -33.78) * mm});
            skLineSegment(sketch, "E12.0.11.0", {"start": v(470.55, 66.22) * mm, "end": v(495.55, 66.22) * mm});
            skLineSegment(sketch, "E12.3.11.0", {"start": v(470.55, 66.22) * mm, "end": v(470.55, -33.78) * mm});
            skLineSegment(sketch, "E12.6.11.0", {"start": v(470.55, -33.78) * mm, "end": v(495.55, -33.78) * mm});
            skLineSegment(sketch, "E12.9.11.0", {"start": v(495.55, 66.22) * mm, "end": v(495.55, -33.78) * mm});
            skLineSegment(sketch, "E13.0.12.0", {"start": v(510.55, 66.22) * mm, "end": v(535.55, 66.22) * mm});
            skLineSegment(sketch, "E13.3.12.0", {"start": v(510.55, 66.22) * mm, "end": v(510.55, -33.78) * mm});
            skLineSegment(sketch, "E13.6.12.0", {"start": v(510.55, -33.78) * mm, "end": v(535.55, -33.78) * mm});
            skLineSegment(sketch, "E13.9.12.0", {"start": v(535.55, 66.22) * mm, "end": v(535.55, -33.78) * mm});
            skLineSegment(sketch, "E13.0.13.0", {"start": v(550.55, 66.22) * mm, "end": v(575.55, 66.22) * mm});
            skLineSegment(sketch, "E13.3.13.0", {"start": v(550.55, 66.22) * mm, "end": v(550.55, -33.78) * mm});
            skLineSegment(sketch, "E13.6.13.0", {"start": v(550.55, -33.78) * mm, "end": v(575.55, -33.78) * mm});
            skLineSegment(sketch, "E13.9.13.0", {"start": v(575.55, 66.22) * mm, "end": v(575.55, -33.78) * mm});
            skLineSegment(sketch, "E13.0.14.0", {"start": v(590.55, 66.22) * mm, "end": v(615.55, 66.22) * mm});
            skLineSegment(sketch, "E13.3.14.0", {"start": v(590.55, 66.22) * mm, "end": v(590.55, -33.78) * mm});
            skLineSegment(sketch, "E13.6.14.0", {"start": v(590.55, -33.78) * mm, "end": v(615.55, -33.78) * mm});
            skLineSegment(sketch, "E13.9.14.0", {"start": v(615.55, 66.22) * mm, "end": v(615.55, -33.78) * mm});
            skLineSegment(sketch, "E14.0.15.0", {"start": v(630.55, 66.22) * mm, "end": v(655.55, 66.22) * mm});
            skLineSegment(sketch, "E14.3.15.0", {"start": v(630.55, 66.22) * mm, "end": v(630.55, -33.78) * mm});
            skLineSegment(sketch, "E14.6.15.0", {"start": v(630.55, -33.78) * mm, "end": v(655.55, -33.78) * mm});
            skLineSegment(sketch, "E14.9.15.0", {"start": v(655.55, 66.22) * mm, "end": v(655.55, -33.78) * mm});
            skLineSegment(sketch, "E14.0.16.0", {"start": v(670.55, 66.22) * mm, "end": v(695.55, 66.22) * mm});
            skLineSegment(sketch, "E14.3.16.0", {"start": v(670.55, 66.22) * mm, "end": v(670.55, -33.78) * mm});
            skLineSegment(sketch, "E14.6.16.0", {"start": v(670.55, -33.78) * mm, "end": v(695.55, -33.78) * mm});
            skLineSegment(sketch, "E14.9.16.0", {"start": v(695.55, 66.22) * mm, "end": v(695.55, -33.78) * mm});
            skLineSegment(sketch, "E14.0.17.0", {"start": v(710.55, 66.22) * mm, "end": v(735.55, 66.22) * mm});
            skLineSegment(sketch, "E14.3.17.0", {"start": v(710.55, 66.22) * mm, "end": v(710.55, -33.78) * mm});
            skLineSegment(sketch, "E14.6.17.0", {"start": v(710.55, -33.78) * mm, "end": v(735.55, -33.78) * mm});
            skLineSegment(sketch, "E14.9.17.0", {"start": v(735.55, 66.22) * mm, "end": v(735.55, -33.78) * mm});
            skLineSegment(sketch, "E14.0.18.0", {"start": v(750.55, 66.22) * mm, "end": v(775.55, 66.22) * mm});
            skLineSegment(sketch, "E14.3.18.0", {"start": v(750.55, 66.22) * mm, "end": v(750.55, -33.78) * mm});
            skLineSegment(sketch, "E14.6.18.0", {"start": v(750.55, -33.78) * mm, "end": v(775.55, -33.78) * mm});
            skLineSegment(sketch, "E14.9.18.0", {"start": v(775.55, 66.22) * mm, "end": v(775.55, -33.78) * mm});
            skSolve(sketch);
        }
        {
            var Q0;
            {Q0=qUnion([makeQuery(id+"F0.imprint","IMPRINT",FACE,{"disambiguationData":[TD([[makeQuery(id+"F0.imprint","IMPRINT",EDGE,{"derivedFrom":sQuery(id+"F0.wireOp",EDGE,"E0.bottom")}),-1.0]])]}),makeQuery(id+"F0.imprint","IMPRINT",FACE,{"disambiguationData":[TD([[makeQuery(id+"F0.imprint","IMPRINT",EDGE,{"derivedFrom":sQuery(id+"F0.wireOp",EDGE,"E5.1.0.0")}),-1.0]])]}),makeQuery(id+"F0.imprint","IMPRINT",FACE,{"disambiguationData":[TD([[makeQuery(id+"F0.imprint","IMPRINT",EDGE,{"derivedFrom":sQuery(id+"F0.wireOp",EDGE,"E5.2.0.0")}),-1.0]])]}),makeQuery(id+"F0.imprint","IMPRINT",FACE,{"disambiguationData":[TD([[makeQuery(id+"F0.imprint","IMPRINT",EDGE,{"derivedFrom":sQuery(id+"F0.wireOp",EDGE,"E6.0.3.0")}),-1.0]])]}),makeQuery(id+"F0.imprint","IMPRINT",FACE,{"disambiguationData":[TD([[makeQuery(id+"F0.imprint","IMPRINT",EDGE,{"derivedFrom":sQuery(id+"F0.wireOp",EDGE,"E6.0.4.0")}),-1.0]])]}),makeQuery(id+"F0.imprint","IMPRINT",FACE,{"disambiguationData":[TD([[makeQuery(id+"F0.imprint","IMPRINT",EDGE,{"derivedFrom":sQuery(id+"F0.wireOp",EDGE,"E6.0.5.0")}),-1.0]])]}),makeQuery(id+"F0.imprint","IMPRINT",FACE,{"disambiguationData":[TD([[makeQuery(id+"F0.imprint","IMPRINT",EDGE,{"derivedFrom":sQuery(id+"F0.wireOp",EDGE,"E6.0.6.0")}),-1.0]])]}),makeQuery(id+"F0.imprint","IMPRINT",FACE,{"disambiguationData":[TD([[makeQuery(id+"F0.imprint","IMPRINT",EDGE,{"derivedFrom":sQuery(id+"F0.wireOp",EDGE,"E6.0.7.0")}),-1.0]])]}),makeQuery(id+"F0.imprint","IMPRINT",FACE,{"disambiguationData":[TD([[makeQuery(id+"F0.imprint","IMPRINT",EDGE,{"derivedFrom":sQuery(id+"F0.wireOp",EDGE,"E6.0.8.0")}),-1.0]])]}),makeQuery(id+"F0.imprint","IMPRINT",FACE,{"disambiguationData":[TD([[makeQuery(id+"F0.imprint","IMPRINT",EDGE,{"derivedFrom":sQuery(id+"F0.wireOp",EDGE,"E6.0.9.0")}),-1.0]])]}),makeQuery(id+"F0.imprint","IMPRINT",FACE,{"disambiguationData":[TD([[makeQuery(id+"F0.imprint","IMPRINT",EDGE,{"derivedFrom":sQuery(id+"F0.wireOp",EDGE,"E6.0.10.0")}),-1.0]])]}),makeQuery(id+"F0.imprint","IMPRINT",FACE,{"disambiguationData":[TD([[makeQuery(id+"F0.imprint","IMPRINT",EDGE,{"derivedFrom":sQuery(id+"F0.wireOp",EDGE,"E6.0.11.0")}),-1.0]])]}),makeQuery(id+"F0.imprint","IMPRINT",FACE,{"disambiguationData":[TD([[makeQuery(id+"F0.imprint","IMPRINT",EDGE,{"derivedFrom":sQuery(id+"F0.wireOp",EDGE,"E7.0.12.0")}),-1.0]])]}),makeQuery(id+"F0.imprint","IMPRINT",FACE,{"disambiguationData":[TD([[makeQuery(id+"F0.imprint","IMPRINT",EDGE,{"derivedFrom":sQuery(id+"F0.wireOp",EDGE,"E8.0.13.0")}),-1.0]])]}),makeQuery(id+"F0.imprint","IMPRINT",FACE,{"disambiguationData":[TD([[makeQuery(id+"F0.imprint","IMPRINT",EDGE,{"derivedFrom":sQuery(id+"F0.wireOp",EDGE,"E8.0.14.0")}),-1.0]])]}),makeQuery(id+"F0.imprint","IMPRINT",FACE,{"disambiguationData":[TD([[makeQuery(id+"F0.imprint","IMPRINT",EDGE,{"derivedFrom":sQuery(id+"F0.wireOp",EDGE,"E9.0.15.0")}),-1.0]])]}),makeQuery(id+"F0.imprint","IMPRINT",FACE,{"disambiguationData":[TD([[makeQuery(id+"F0.imprint","IMPRINT",EDGE,{"derivedFrom":sQuery(id+"F0.wireOp",EDGE,"E9.0.16.0")}),-1.0]])]}),makeQuery(id+"F0.imprint","IMPRINT",FACE,{"disambiguationData":[TD([[makeQuery(id+"F0.imprint","IMPRINT",EDGE,{"derivedFrom":sQuery(id+"F0.wireOp",EDGE,"E9.0.17.0")}),-1.0]])]}),makeQuery(id+"F0.imprint","IMPRINT",FACE,{"disambiguationData":[TD([[makeQuery(id+"F0.imprint","IMPRINT",EDGE,{"derivedFrom":sQuery(id+"F0.wireOp",EDGE,"E9.0.18.0")}),-1.0]])]})]);}
            extrude(context, id + "F2", {"entities" : qUnion([Q0]), "depth" : 7 * mm, "offsetDistance" : 25 * mm});
        }
        {
            var Q0;
            Q0=qSketchRegion(id+"F1",true);
            extrude(context, id + "F3", {"entities" : qUnion([Q0]), "operationType" : NewBodyOperationType.ADD, "oppositeDirection" : true, "depth" : 1.5 * mm, "offsetDistance" : 25 * mm});
        }
        {
            var Q0;
            Q0=makeQuery(id+"F2.opExtrude","CAP_FACE",FACE,{"disambiguationData":[OSD([sQuery(id+"F0.wireOp",EDGE,"E0.bottom"),sQuery(id+"F0.wireOp",EDGE,"E0.top"),sQuery(id+"F0.wireOp",EDGE,"E0.left"),sQuery(id+"F0.wireOp",EDGE,"E0.right"),sQuery(id+"F0.wireOp",EDGE,"E1.bottom"),sQuery(id+"F0.wireOp",EDGE,"E1.top"),sQuery(id+"F0.wireOp",EDGE,"E1.left"),sQuery(id+"F0.wireOp",EDGE,"E1.right"),sQuery(id+"F0.wireOp",EDGE,"E2.bottom"),sQuery(id+"F0.wireOp",EDGE,"E2.top"),sQuery(id+"F0.wireOp",EDGE,"E3.bottom"),sQuery(id+"F0.wireOp",EDGE,"E3.top"),sQuery(id+"F0.wireOp",EDGE,"E3.left"),sQuery(id+"F0.wireOp",EDGE,"E3.right")])],"isStart":false});
            var sketch = newSketch(context, id + "F4", { "sketchPlane" : qUnion([Q0])});
            skText(sketch, "E15", { "text": "1/8x40", "fontName": "OpenSans-Regular.ttf"});
            const initialGuessF4  = {"E15": [0.03418, 0.05922, 1, 0, 0.004]};
            skSetInitialGuess(sketch, initialGuessF4);
            skSolve(sketch);
        }
        {
            var Q0;
            Q0=makeQuery(id+"F2.opExtrude","CAP_FACE",FACE,{"disambiguationData":[OSD([sQuery(id+"F0.wireOp",EDGE,"E5.1.0.0"),sQuery(id+"F0.wireOp",EDGE,"E5.1.0.1"),sQuery(id+"F0.wireOp",EDGE,"E5.1.0.2"),sQuery(id+"F0.wireOp",EDGE,"E5.1.0.3"),sQuery(id+"F0.wireOp",EDGE,"E5.1.0.4"),sQuery(id+"F0.wireOp",EDGE,"E5.1.0.5"),sQuery(id+"F0.wireOp",EDGE,"E5.1.0.7"),sQuery(id+"F0.wireOp",EDGE,"E5.1.0.8"),sQuery(id+"F0.wireOp",EDGE,"E5.1.0.10"),sQuery(id+"F0.wireOp",EDGE,"E5.1.0.11"),sQuery(id+"F0.wireOp",EDGE,"E5.1.0.12"),sQuery(id+"F0.wireOp",EDGE,"E5.1.0.13")])],"isStart":false});
            var sketch = newSketch(context, id + "F5", { "sketchPlane" : qUnion([Q0])});
            skText(sketch, "E16", { "text": "5/32x32", "fontName": "OpenSans-Regular.ttf"});
            const initialGuessF5  = {"E16": [0.0726, 0.05922, 1, 0, 0.004]};
            skSetInitialGuess(sketch, initialGuessF5);
            skSolve(sketch);
        }
        {
            var Q0;
            Q0=makeQuery(id+"F2.opExtrude","CAP_FACE",FACE,{"disambiguationData":[OSD([sQuery(id+"F0.wireOp",EDGE,"E5.2.0.0"),sQuery(id+"F0.wireOp",EDGE,"E5.2.0.1"),sQuery(id+"F0.wireOp",EDGE,"E5.2.0.2"),sQuery(id+"F0.wireOp",EDGE,"E5.2.0.3"),sQuery(id+"F0.wireOp",EDGE,"E5.2.0.4"),sQuery(id+"F0.wireOp",EDGE,"E5.2.0.5"),sQuery(id+"F0.wireOp",EDGE,"E5.2.0.7"),sQuery(id+"F0.wireOp",EDGE,"E5.2.0.8"),sQuery(id+"F0.wireOp",EDGE,"E5.2.0.10"),sQuery(id+"F0.wireOp",EDGE,"E5.2.0.11"),sQuery(id+"F0.wireOp",EDGE,"E5.2.0.12"),sQuery(id+"F0.wireOp",EDGE,"E5.2.0.13")])],"isStart":false});
            var sketch = newSketch(context, id + "F6", { "sketchPlane" : qUnion([Q0])});
            skText(sketch, "E17", { "text": "5/32x40", "fontName": "OpenSans-Regular.ttf"});
            const initialGuessF6  = {"E17": [0.1126, 0.05922, 1, 0, 0.004]};
            skSetInitialGuess(sketch, initialGuessF6);
            skSolve(sketch);
        }
        {
            var Q0;
            Q0=makeQuery(id+"F2.opExtrude","CAP_FACE",FACE,{"disambiguationData":[OSD([sQuery(id+"F0.wireOp",EDGE,"E6.0.3.0"),sQuery(id+"F0.wireOp",EDGE,"E6.3.3.0"),sQuery(id+"F0.wireOp",EDGE,"E6.6.3.0"),sQuery(id+"F0.wireOp",EDGE,"E6.9.3.0"),sQuery(id+"F0.wireOp",EDGE,"E6.12.3.0"),sQuery(id+"F0.wireOp",EDGE,"E6.15.3.0"),sQuery(id+"F0.wireOp",EDGE,"E6.21.3.0"),sQuery(id+"F0.wireOp",EDGE,"E6.24.3.0"),sQuery(id+"F0.wireOp",EDGE,"E6.30.3.0"),sQuery(id+"F0.wireOp",EDGE,"E6.33.3.0"),sQuery(id+"F0.wireOp",EDGE,"E6.36.3.0"),sQuery(id+"F0.wireOp",EDGE,"E6.39.3.0")])],"isStart":false});
            var sketch = newSketch(context, id + "F7", { "sketchPlane" : qUnion([Q0])});
            skText(sketch, "E18", { "text": "3/16x32", "fontName": "OpenSans-Regular.ttf"});
            const initialGuessF7  = {"E18": [0.1526, 0.05922, 1, 0, 0.004]};
            skSetInitialGuess(sketch, initialGuessF7);
            skSolve(sketch);
        }
        {
            var Q0;
            Q0=makeQuery(id+"F2.opExtrude","CAP_FACE",FACE,{"disambiguationData":[OSD([sQuery(id+"F0.wireOp",EDGE,"E6.0.4.0"),sQuery(id+"F0.wireOp",EDGE,"E6.3.4.0"),sQuery(id+"F0.wireOp",EDGE,"E6.6.4.0"),sQuery(id+"F0.wireOp",EDGE,"E6.9.4.0"),sQuery(id+"F0.wireOp",EDGE,"E6.12.4.0"),sQuery(id+"F0.wireOp",EDGE,"E6.15.4.0"),sQuery(id+"F0.wireOp",EDGE,"E6.21.4.0"),sQuery(id+"F0.wireOp",EDGE,"E6.24.4.0"),sQuery(id+"F0.wireOp",EDGE,"E6.30.4.0"),sQuery(id+"F0.wireOp",EDGE,"E6.33.4.0"),sQuery(id+"F0.wireOp",EDGE,"E6.36.4.0"),sQuery(id+"F0.wireOp",EDGE,"E6.39.4.0")])],"isStart":false});
            var sketch = newSketch(context, id + "F8", { "sketchPlane" : qUnion([Q0])});
            skText(sketch, "E19", { "text": "3/16x40", "fontName": "OpenSans-Regular.ttf"});
            const initialGuessF8  = {"E19": [0.1926, 0.05922, 1, 0, 0.004]};
            skSetInitialGuess(sketch, initialGuessF8);
            skSolve(sketch);
        }
        {
            var Q0;
            Q0=makeQuery(id+"F2.opExtrude","CAP_FACE",FACE,{"disambiguationData":[OSD([sQuery(id+"F0.wireOp",EDGE,"E6.0.5.0"),sQuery(id+"F0.wireOp",EDGE,"E6.3.5.0"),sQuery(id+"F0.wireOp",EDGE,"E6.6.5.0"),sQuery(id+"F0.wireOp",EDGE,"E6.9.5.0"),sQuery(id+"F0.wireOp",EDGE,"E6.12.5.0"),sQuery(id+"F0.wireOp",EDGE,"E6.15.5.0"),sQuery(id+"F0.wireOp",EDGE,"E6.21.5.0"),sQuery(id+"F0.wireOp",EDGE,"E6.24.5.0"),sQuery(id+"F0.wireOp",EDGE,"E6.30.5.0"),sQuery(id+"F0.wireOp",EDGE,"E6.33.5.0"),sQuery(id+"F0.wireOp",EDGE,"E6.36.5.0"),sQuery(id+"F0.wireOp",EDGE,"E6.39.5.0")])],"isStart":false});
            var sketch = newSketch(context, id + "F9", { "sketchPlane" : qUnion([Q0])});
            skText(sketch, "E20", { "text": "7/32x32", "fontName": "OpenSans-Regular.ttf"});
            skText(sketch, "E21", { "text": "7/32x40", "fontName": "OpenSans-Regular.ttf"});
            skText(sketch, "E22", { "text": "1/4x32", "fontName": "OpenSans-Regular.ttf"});
            skText(sketch, "E23", { "text": "1/4x40", "fontName": "OpenSans-Regular.ttf"});
            skText(sketch, "E24", { "text": "9/32x32", "fontName": "OpenSans-Regular.ttf"});
            skText(sketch, "E25", { "text": "9/32x40", "fontName": "OpenSans-Regular.ttf"});
            skText(sketch, "E26", { "text": "5/16x32", "fontName": "OpenSans-Regular.ttf"});
            skText(sketch, "E27", { "text": "5/16x40", "fontName": "OpenSans-Regular.ttf"});
            skText(sketch, "E28", { "text": "3/8x32", "fontName": "OpenSans-Regular.ttf"});
            skText(sketch, "E29", { "text": "3/8x40", "fontName": "OpenSans-Regular.ttf"});
            skText(sketch, "E30", { "text": "7/16x32", "fontName": "OpenSans-Regular.ttf"});
            skText(sketch, "E31", { "text": "7/16x40", "fontName": "OpenSans-Regular.ttf"});
            skText(sketch, "E32", { "text": "1/2x32", "fontName": "OpenSans-Regular.ttf"});
            skText(sketch, "E33", { "text": "1/2x40", "fontName": "OpenSans-Regular.ttf"});
            const initialGuessF9  = {"E20": [0.2326, 0.05922, 1, 0, 0.004], "E21": [0.2726, 0.05922, 1, 0, 0.004], "E22": [0.3142, 0.05922, 1, 0, 0.004], "E23": [0.35418, 0.05922, 1, 0, 0.004], "E24": [0.3926, 0.05922, 1, 0, 0.004], "E25": [0.4326, 0.05922, 1, 0, 0.004], "E26": [0.4726, 0.05922, 1, 0, 0.004], "E27": [0.5126, 0.05922, 1, 0, 0.004], "E28": [0.5542, 0.05922, 1, 0, 0.004], "E29": [0.59418, 0.05922, 1, 0, 0.004], "E30": [0.6326, 0.05922, 1, 0, 0.004], "E31": [0.6726, 0.05922, 1, 0, 0.004], "E32": [0.7142, 0.05922, 1, 0, 0.004], "E33": [0.75418, 0.05922, 1, 0, 0.004]};
            skSetInitialGuess(sketch, initialGuessF9);
            skSolve(sketch);
        }
        {
            var Q0;
            Q0=makeQuery(id+"F4.imprint","IMPRINT",FACE,{"disambiguationData":[TD([[makeQuery(id+"F4.imprint","IMPRINT",EDGE,{"derivedFrom":sQuery(id+"F4.wireOp",EDGE,"E15.sketch_text.stroke-0")}),-1.0]])]});
            var Q1;
            Q1=makeQuery(id+"F4.imprint","IMPRINT",FACE,{"disambiguationData":[TD([[makeQuery(id+"F4.imprint","IMPRINT",EDGE,{"derivedFrom":sQuery(id+"F4.wireOp",EDGE,"E15.sketch_text.stroke-9")}),-1.0]])]});
            var Q2;
            Q2=makeQuery(id+"F4.imprint","IMPRINT",FACE,{"disambiguationData":[TD([[makeQuery(id+"F4.imprint","IMPRINT",EDGE,{"derivedFrom":sQuery(id+"F4.wireOp",EDGE,"E15.sketch_text.stroke-44")}),-1.0]])]});
            var Q3;
            Q3=makeQuery(id+"F4.imprint","IMPRINT",FACE,{"disambiguationData":[TD([[makeQuery(id+"F4.imprint","IMPRINT",EDGE,{"derivedFrom":sQuery(id+"F4.wireOp",EDGE,"E15.sketch_text.stroke-56")}),-1.0]])]});
            var Q4;
            Q4=makeQuery(id+"F4.imprint","IMPRINT",FACE,{"disambiguationData":[TD([[makeQuery(id+"F4.imprint","IMPRINT",EDGE,{"derivedFrom":sQuery(id+"F4.wireOp",EDGE,"E15.sketch_text.stroke-73")}),-1.0]])]});
            var Q5;
            Q5=makeQuery(id+"F4.imprint","IMPRINT",FACE,{"disambiguationData":[TD([[makeQuery(id+"F4.imprint","IMPRINT",EDGE,{"derivedFrom":sQuery(id+"F4.wireOp",EDGE,"E15.sketch_text.stroke-13")}),-1.0]])]});
            var Q6;
            Q6=makeQuery(id+"F5.imprint","IMPRINT",FACE,{"disambiguationData":[TD([[makeQuery(id+"F5.imprint","IMPRINT",EDGE,{"derivedFrom":sQuery(id+"F5.wireOp",EDGE,"E16.sketch_text.stroke-0")}),-1.0]])]});
            var Q7;
            Q7=makeQuery(id+"F5.imprint","IMPRINT",FACE,{"disambiguationData":[TD([[makeQuery(id+"F5.imprint","IMPRINT",EDGE,{"derivedFrom":sQuery(id+"F5.wireOp",EDGE,"E16.sketch_text.stroke-19")}),-1.0]])]});
            var Q8;
            Q8=makeQuery(id+"F5.imprint","IMPRINT",FACE,{"disambiguationData":[TD([[makeQuery(id+"F5.imprint","IMPRINT",EDGE,{"derivedFrom":sQuery(id+"F5.wireOp",EDGE,"E16.sketch_text.stroke-23")}),-1.0]])]});
            var Q9;
            Q9=makeQuery(id+"F5.imprint","IMPRINT",FACE,{"disambiguationData":[TD([[makeQuery(id+"F5.imprint","IMPRINT",EDGE,{"derivedFrom":sQuery(id+"F5.wireOp",EDGE,"E16.sketch_text.stroke-51")}),-1.0]])]});
            var Q10;
            Q10=makeQuery(id+"F5.imprint","IMPRINT",FACE,{"disambiguationData":[TD([[makeQuery(id+"F5.imprint","IMPRINT",EDGE,{"derivedFrom":sQuery(id+"F5.wireOp",EDGE,"E16.sketch_text.stroke-71")}),-1.0]])]});
            var Q11;
            Q11=makeQuery(id+"F5.imprint","IMPRINT",FACE,{"disambiguationData":[TD([[makeQuery(id+"F5.imprint","IMPRINT",EDGE,{"derivedFrom":sQuery(id+"F5.wireOp",EDGE,"E16.sketch_text.stroke-83")}),-1.0]])]});
            var Q12;
            Q12=makeQuery(id+"F5.imprint","IMPRINT",FACE,{"disambiguationData":[TD([[makeQuery(id+"F5.imprint","IMPRINT",EDGE,{"derivedFrom":sQuery(id+"F5.wireOp",EDGE,"E16.sketch_text.stroke-111")}),-1.0]])]});
            var Q13;
            Q13=makeQuery(id+"F7.imprint","IMPRINT",FACE,{"disambiguationData":[TD([[makeQuery(id+"F7.imprint","IMPRINT",EDGE,{"derivedFrom":sQuery(id+"F7.wireOp",EDGE,"E18.sketch_text.stroke-0")}),-1.0]])]});
            var Q14;
            Q14=makeQuery(id+"F7.imprint","IMPRINT",FACE,{"disambiguationData":[TD([[makeQuery(id+"F7.imprint","IMPRINT",EDGE,{"derivedFrom":sQuery(id+"F7.wireOp",EDGE,"E18.sketch_text.stroke-28")}),-1.0]])]});
            var Q15;
            Q15=makeQuery(id+"F7.imprint","IMPRINT",FACE,{"disambiguationData":[TD([[makeQuery(id+"F7.imprint","IMPRINT",EDGE,{"derivedFrom":sQuery(id+"F7.wireOp",EDGE,"E18.sketch_text.stroke-32")}),-1.0]])]});
            var Q16;
            Q16=makeQuery(id+"F7.imprint","IMPRINT",FACE,{"disambiguationData":[TD([[makeQuery(id+"F7.imprint","IMPRINT",EDGE,{"derivedFrom":sQuery(id+"F7.wireOp",EDGE,"E18.sketch_text.stroke-66")}),-1.0]])]});
            var Q17;
            Q17=makeQuery(id+"F7.imprint","IMPRINT",FACE,{"disambiguationData":[TD([[makeQuery(id+"F7.imprint","IMPRINT",EDGE,{"derivedFrom":sQuery(id+"F7.wireOp",EDGE,"E18.sketch_text.stroke-78")}),-1.0]])]});
            var Q18;
            Q18=makeQuery(id+"F7.imprint","IMPRINT",FACE,{"disambiguationData":[TD([[makeQuery(id+"F7.imprint","IMPRINT",EDGE,{"derivedFrom":sQuery(id+"F7.wireOp",EDGE,"E18.sketch_text.stroke-106")}),-1.0]])]});
            var Q19;
            Q19=makeQuery(id+"F7.imprint","IMPRINT",FACE,{"disambiguationData":[TD([[makeQuery(id+"F7.imprint","IMPRINT",EDGE,{"derivedFrom":sQuery(id+"F7.wireOp",EDGE,"E18.sketch_text.stroke-41")}),-1.0]])]});
            var Q20;
            Q20=makeQuery(id+"F8.imprint","IMPRINT",FACE,{"disambiguationData":[TD([[makeQuery(id+"F8.imprint","IMPRINT",EDGE,{"derivedFrom":sQuery(id+"F8.wireOp",EDGE,"E19.sketch_text.stroke-0")}),-1.0]])]});
            var Q21;
            Q21=makeQuery(id+"F8.imprint","IMPRINT",FACE,{"disambiguationData":[TD([[makeQuery(id+"F8.imprint","IMPRINT",EDGE,{"derivedFrom":sQuery(id+"F8.wireOp",EDGE,"E19.sketch_text.stroke-28")}),-1.0]])]});
            var Q22;
            Q22=makeQuery(id+"F8.imprint","IMPRINT",FACE,{"disambiguationData":[TD([[makeQuery(id+"F8.imprint","IMPRINT",EDGE,{"derivedFrom":sQuery(id+"F8.wireOp",EDGE,"E19.sketch_text.stroke-32")}),-1.0]])]});
            var Q23;
            Q23=makeQuery(id+"F8.imprint","IMPRINT",FACE,{"disambiguationData":[TD([[makeQuery(id+"F8.imprint","IMPRINT",EDGE,{"derivedFrom":sQuery(id+"F8.wireOp",EDGE,"E19.sketch_text.stroke-66")}),-1.0]])]});
            var Q24;
            Q24=makeQuery(id+"F8.imprint","IMPRINT",FACE,{"disambiguationData":[TD([[makeQuery(id+"F8.imprint","IMPRINT",EDGE,{"derivedFrom":sQuery(id+"F8.wireOp",EDGE,"E19.sketch_text.stroke-41")}),-1.0]])]});
            var Q25;
            Q25=makeQuery(id+"F8.imprint","IMPRINT",FACE,{"disambiguationData":[TD([[makeQuery(id+"F8.imprint","IMPRINT",EDGE,{"derivedFrom":sQuery(id+"F8.wireOp",EDGE,"E19.sketch_text.stroke-78")}),-1.0]])]});
            var Q26;
            Q26=makeQuery(id+"F8.imprint","IMPRINT",FACE,{"disambiguationData":[TD([[makeQuery(id+"F8.imprint","IMPRINT",EDGE,{"derivedFrom":sQuery(id+"F8.wireOp",EDGE,"E19.sketch_text.stroke-95")}),-1.0]])]});
            var Q27;
            Q27=makeQuery(id+"F6.imprint","IMPRINT",FACE,{"disambiguationData":[TD([[makeQuery(id+"F6.imprint","IMPRINT",EDGE,{"derivedFrom":sQuery(id+"F6.wireOp",EDGE,"E17.sketch_text.stroke-0")}),-1.0]])]});
            var Q28;
            Q28=makeQuery(id+"F6.imprint","IMPRINT",FACE,{"disambiguationData":[TD([[makeQuery(id+"F6.imprint","IMPRINT",EDGE,{"derivedFrom":sQuery(id+"F6.wireOp",EDGE,"E17.sketch_text.stroke-19")}),-1.0]])]});
            var Q29;
            Q29=makeQuery(id+"F6.imprint","IMPRINT",FACE,{"disambiguationData":[TD([[makeQuery(id+"F6.imprint","IMPRINT",EDGE,{"derivedFrom":sQuery(id+"F6.wireOp",EDGE,"E17.sketch_text.stroke-23")}),-1.0]])]});
            var Q30;
            Q30=makeQuery(id+"F6.imprint","IMPRINT",FACE,{"disambiguationData":[TD([[makeQuery(id+"F6.imprint","IMPRINT",EDGE,{"derivedFrom":sQuery(id+"F6.wireOp",EDGE,"E17.sketch_text.stroke-51")}),-1.0]])]});
            var Q31;
            Q31=makeQuery(id+"F6.imprint","IMPRINT",FACE,{"disambiguationData":[TD([[makeQuery(id+"F6.imprint","IMPRINT",EDGE,{"derivedFrom":sQuery(id+"F6.wireOp",EDGE,"E17.sketch_text.stroke-71")}),-1.0]])]});
            var Q32;
            Q32=makeQuery(id+"F6.imprint","IMPRINT",FACE,{"disambiguationData":[TD([[makeQuery(id+"F6.imprint","IMPRINT",EDGE,{"derivedFrom":sQuery(id+"F6.wireOp",EDGE,"E17.sketch_text.stroke-83")}),-1.0]])]});
            var Q33;
            Q33=makeQuery(id+"F6.imprint","IMPRINT",FACE,{"disambiguationData":[TD([[makeQuery(id+"F6.imprint","IMPRINT",EDGE,{"derivedFrom":sQuery(id+"F6.wireOp",EDGE,"E17.sketch_text.stroke-100")}),-1.0]])]});
            var Q34;
            Q34 = qSketchRegion(id + "F9", true);
            extrude(context, id + "F10", {"entities" : qUnion([Q0, Q1, Q2, Q3, Q4, Q5, Q6, Q7, Q8, Q9, Q10, Q11, Q12, Q13, Q14, Q15, Q16, Q17, Q18, Q19, Q20, Q21, Q22, Q23, Q24, Q25, Q26, Q27, Q28, Q29, Q30, Q31, Q32, Q33, Q34]), "operationType" : NewBodyOperationType.REMOVE, "oppositeDirection" : true, "depth" : 2 * mm, "offsetDistance" : 25 * mm});
        }
        {
            var Q0;
            Q0=qCreatedBy(makeId("Top.planeOp"),FACE);
            var sketch = newSketch(context, id + "F11", { "sketchPlane" : qUnion([Q0])});
            skLineSegment(sketch, "E34.bottom", {"start": v(282.97, -45.7) * mm, "end": v(363.17, -45.7) * mm});
            skLineSegment(sketch, "E34.top", {"start": v(282.97, -165.7) * mm, "end": v(363.17, -165.7) * mm});
            skLineSegment(sketch, "E34.left", {"start": v(282.97, -45.7) * mm, "end": v(282.97, -165.7) * mm});
            skLineSegment(sketch, "E34.right", {"start": v(363.17, -45.7) * mm, "end": v(363.17, -165.7) * mm});
            skLineSegment(sketch, "E35.bottom", {"start": v(309.37, -45.7) * mm, "end": v(310.37, -45.7) * mm});
            skLineSegment(sketch, "E35.top", {"start": v(309.37, -165.7) * mm, "end": v(310.37, -165.7) * mm});
            skLineSegment(sketch, "E35.left", {"start": v(309.37, -45.7) * mm, "end": v(309.37, -165.7) * mm});
            skLineSegment(sketch, "E35.right", {"start": v(310.37, -45.7) * mm, "end": v(310.37, -165.7) * mm});
            skLineSegment(sketch, "E36.bottom", {"start": v(335.77, -45.7) * mm, "end": v(336.77, -45.7) * mm});
            skLineSegment(sketch, "E36.top", {"start": v(335.77, -165.7) * mm, "end": v(336.77, -165.7) * mm});
            skLineSegment(sketch, "E36.left", {"start": v(335.77, -45.7) * mm, "end": v(335.77, -165.7) * mm});
            skLineSegment(sketch, "E36.right", {"start": v(336.77, -45.7) * mm, "end": v(336.77, -165.7) * mm});
            skLineSegment(sketch, "E37.bottom", {"start": v(363.17, -45.7) * mm, "end": v(362.17, -45.7) * mm});
            skLineSegment(sketch, "E37.top", {"start": v(363.17, -165.7) * mm, "end": v(362.17, -165.7) * mm});
            skLineSegment(sketch, "E37.right", {"start": v(362.17, -45.7) * mm, "end": v(362.17, -165.7) * mm});
            skLineSegment(sketch, "E38.bottom", {"start": v(282.97, -45.7) * mm, "end": v(283.97, -45.7) * mm});
            skLineSegment(sketch, "E38.top", {"start": v(282.97, -165.7) * mm, "end": v(283.97, -165.7) * mm});
            skLineSegment(sketch, "E38.right", {"start": v(283.97, -45.7) * mm, "end": v(283.97, -165.7) * mm});
            skLineSegment(sketch, "E39", {"start": v(284.17, -45.7) * mm, "end": v(284.17, -165.7) * mm, "construction": true});
            skLineSegment(sketch, "E40", {"start": v(309.17, -45.7) * mm, "end": v(309.17, -165.7) * mm, "construction": true});
            skLineSegment(sketch, "E41", {"start": v(284.17, -112.21) * mm, "end": v(309.17, -112.21) * mm, "construction": true});
            skLineSegment(sketch, "E42", {"start": v(335.57, -45.7) * mm, "end": v(335.57, -119.57) * mm, "construction": true});
            skLineSegment(sketch, "E43", {"start": v(310.57, -45.7) * mm, "end": v(310.57, -165.7) * mm, "construction": true});
            skLineSegment(sketch, "E44", {"start": v(336.97, -45.7) * mm, "end": v(336.97, -165.7) * mm, "construction": true});
            skLineSegment(sketch, "E45", {"start": v(361.97, -45.7) * mm, "end": v(361.97, -165.7) * mm, "construction": true});
            skLineSegment(sketch, "E46", {"start": v(310.57, -111.1) * mm, "end": v(335.57, -111.1) * mm, "construction": true});
            skLineSegment(sketch, "E47", {"start": v(336.97, -111.1) * mm, "end": v(361.97, -111.1) * mm, "construction": true});
            skLineSegment(sketch, "E48", {"start": v(363.17, -45.7) * mm, "end": v(388.57, -45.7) * mm});
            skLineSegment(sketch, "E49", {"start": v(388.57, -45.7) * mm, "end": v(388.57, -165.7) * mm});
            skLineSegment(sketch, "E50", {"start": v(388.57, -165.7) * mm, "end": v(363.17, -165.7) * mm});
            skLineSegment(sketch, "E51", {"start": v(388.37, -165.7) * mm, "end": v(388.37, -45.7) * mm, "construction": true});
            skLineSegment(sketch, "E52", {"start": v(363.37, -45.7) * mm, "end": v(363.37, -165.7) * mm, "construction": true});
            skLineSegment(sketch, "E53", {"start": v(363.37, -93.33) * mm, "end": v(388.37, -93.33) * mm, "construction": true});
            skLineSegment(sketch, "E54", {"start": v(388.57, -45.7) * mm, "end": v(389.57, -45.7) * mm});
            skLineSegment(sketch, "E55", {"start": v(389.57, -45.7) * mm, "end": v(389.57, -165.7) * mm});
            skLineSegment(sketch, "E56", {"start": v(389.57, -165.7) * mm, "end": v(388.57, -165.7) * mm});
            skSolve(sketch);
        }
        {
            var Q0;
            {var subQ2=sQuery(id+"F11.wireOp",EDGE,"E34.left");Q0=makeQuery(id+"F11.imprint","IMPRINT",FACE,{"disambiguationData":[TD([[makeQuery(id+"F11.imprint","IMPRINT",EDGE,{"derivedFrom":subQ2}),1.0]])]});}
            var Q1;
            {var subQ2=sQuery(id+"F11.wireOp",EDGE,"E35.left");Q1=makeQuery(id+"F11.imprint","IMPRINT",FACE,{"disambiguationData":[TD([[makeQuery(id+"F11.imprint","IMPRINT",EDGE,{"derivedFrom":subQ2}),-1.0]])]});}
            var Q2;
            {var subQ2=sQuery(id+"F11.wireOp",EDGE,"E35.left");Q2=makeQuery(id+"F11.imprint","IMPRINT",FACE,{"disambiguationData":[TD([[makeQuery(id+"F11.imprint","IMPRINT",EDGE,{"derivedFrom":subQ2}),1.0]])]});}
            var Q3;
            {var subQ0=sQuery(id+"F11.wireOp",EDGE,"E35.right");Q3=makeQuery(id+"F11.imprint","IMPRINT",FACE,{"disambiguationData":[TD([[makeQuery(id+"F11.imprint","IMPRINT",EDGE,{"derivedFrom":subQ0}),1.0]])]});}
            var Q4;
            {var subQ0=sQuery(id+"F11.wireOp",EDGE,"E36.left");Q4=makeQuery(id+"F11.imprint","IMPRINT",FACE,{"disambiguationData":[TD([[makeQuery(id+"F11.imprint","IMPRINT",EDGE,{"derivedFrom":subQ0}),1.0]])]});}
            var Q5;
            {var subQ0=sQuery(id+"F11.wireOp",EDGE,"E36.right");Q5=makeQuery(id+"F11.imprint","IMPRINT",FACE,{"disambiguationData":[TD([[makeQuery(id+"F11.imprint","IMPRINT",EDGE,{"derivedFrom":subQ0}),1.0]])]});}
            var Q6;
            {var subQ0=sQuery(id+"F11.wireOp",EDGE,"E34.right");Q6=makeQuery(id+"F11.imprint","IMPRINT",FACE,{"disambiguationData":[TD([[makeQuery(id+"F11.imprint","IMPRINT",EDGE,{"derivedFrom":subQ0}),-1.0]])]});}
            var Q7;
            Q7=makeQuery(id+"F11.imprint","IMPRINT",FACE,{"disambiguationData":[TD([[makeQuery(id+"F11.imprint","IMPRINT",EDGE,{"derivedFrom":sQuery(id+"F11.wireOp",EDGE,"E34.right")}),1.0]])]});
            var Q8;
            Q8=makeQuery(id+"F11.imprint","IMPRINT",FACE,{"disambiguationData":[TD([[makeQuery(id+"F11.imprint","IMPRINT",EDGE,{"derivedFrom":sQuery(id+"F11.wireOp",EDGE,"E49")}),1.0]])]});
            extrude(context, id + "F12", {"entities" : qUnion([Q0, Q1, Q2, Q3, Q4, Q5, Q6, Q7, Q8]), "depth" : 1 * mm, "offsetDistance" : 25 * mm});
        }
        {
            var Q0;
            {var subQ2=sQuery(id+"F11.wireOp",EDGE,"E34.left");Q0=makeQuery(id+"F11.imprint","IMPRINT",FACE,{"disambiguationData":[TD([[makeQuery(id+"F11.imprint","IMPRINT",EDGE,{"derivedFrom":subQ2}),1.0]])]});}
            var Q1;
            {var subQ2=sQuery(id+"F11.wireOp",EDGE,"E35.left");Q1=makeQuery(id+"F11.imprint","IMPRINT",FACE,{"disambiguationData":[TD([[makeQuery(id+"F11.imprint","IMPRINT",EDGE,{"derivedFrom":subQ2}),1.0]])]});}
            var Q2;
            {var subQ0=sQuery(id+"F11.wireOp",EDGE,"E36.left");Q2=makeQuery(id+"F11.imprint","IMPRINT",FACE,{"disambiguationData":[TD([[makeQuery(id+"F11.imprint","IMPRINT",EDGE,{"derivedFrom":subQ0}),1.0]])]});}
            var Q3;
            {var subQ0=sQuery(id+"F11.wireOp",EDGE,"E34.right");Q3=makeQuery(id+"F11.imprint","IMPRINT",FACE,{"disambiguationData":[TD([[makeQuery(id+"F11.imprint","IMPRINT",EDGE,{"derivedFrom":subQ0}),-1.0]])]});}
            var Q4;
            Q4=makeQuery(id+"F11.imprint","IMPRINT",FACE,{"disambiguationData":[TD([[makeQuery(id+"F11.imprint","IMPRINT",EDGE,{"derivedFrom":sQuery(id+"F11.wireOp",EDGE,"E49")}),1.0]])]});
            extrude(context, id + "F13", {"entities" : qUnion([Q0, Q1, Q2, Q3, Q4]), "operationType" : NewBodyOperationType.ADD, "depth" : 10 * mm, "offsetDistance" : 25 * mm});
        }
        {
            var Q0;
            Q0=makeQuery(id+"F13.opExtrude","SWEPT_FACE",FACE,{"disambiguationData":[OSD([sQuery(id+"F11.wireOp",EDGE,"E38.right")])]});
            var sketch = newSketch(context, id + "F14", { "sketchPlane" : qUnion([Q0])});
            skLineSegment(sketch, "E57", {"start": v(-60.3, 1) * mm, "end": v(-47.45, 10) * mm});
            skLineSegment(sketch, "E58", {"start": v(-47.45, 10) * mm, "end": v(-45.7, 10) * mm});
            skLineSegment(sketch, "E59", {"start": v(-45.7, 10) * mm, "end": v(-58.56, 1) * mm});
            skLineSegment(sketch, "E60", {"start": v(-58.56, 1) * mm, "end": v(-60.3, 1) * mm});
            skLineSegment(sketch, "E61.1.0.0", {"start": v(-79.48, 1) * mm, "end": v(-66.62, 10) * mm});
            skLineSegment(sketch, "E61.1.0.1", {"start": v(-64.88, 10) * mm, "end": v(-77.73, 1) * mm});
            skLineSegment(sketch, "E61.1.0.2", {"start": v(-66.62, 10) * mm, "end": v(-64.88, 10) * mm});
            skLineSegment(sketch, "E61.1.0.3", {"start": v(-77.73, 1) * mm, "end": v(-79.48, 1) * mm});
            skLineSegment(sketch, "E61.2.0.0", {"start": v(-98.65, 1) * mm, "end": v(-85.8, 10) * mm});
            skLineSegment(sketch, "E61.2.0.1", {"start": v(-84.06, 10) * mm, "end": v(-96.91, 1) * mm});
            skLineSegment(sketch, "E61.2.0.2", {"start": v(-85.8, 10) * mm, "end": v(-84.06, 10) * mm});
            skLineSegment(sketch, "E61.2.0.3", {"start": v(-96.91, 1) * mm, "end": v(-98.65, 1) * mm});
            skLineSegment(sketch, "E61.direction1", {"start": v(-60.3, 1) * mm, "end": v(-79.48, 1) * mm, "construction": true});
            skLineSegment(sketch, "E62.0.3.0", {"start": v(-117.83, 1) * mm, "end": v(-104.98, 10) * mm});
            skLineSegment(sketch, "E62.3.3.0", {"start": v(-103.24, 10) * mm, "end": v(-116.09, 1) * mm});
            skLineSegment(sketch, "E62.6.3.0", {"start": v(-104.98, 10) * mm, "end": v(-103.24, 10) * mm});
            skLineSegment(sketch, "E62.9.3.0", {"start": v(-116.09, 1) * mm, "end": v(-117.83, 1) * mm});
            skLineSegment(sketch, "E63.0.4.0", {"start": v(-137.01, 1) * mm, "end": v(-124.16, 10) * mm});
            skLineSegment(sketch, "E63.3.4.0", {"start": v(-122.41, 10) * mm, "end": v(-135.27, 1) * mm});
            skLineSegment(sketch, "E63.6.4.0", {"start": v(-124.16, 10) * mm, "end": v(-122.41, 10) * mm});
            skLineSegment(sketch, "E63.9.4.0", {"start": v(-135.27, 1) * mm, "end": v(-137.01, 1) * mm});
            skLineSegment(sketch, "E63.0.5.0", {"start": v(-156.19, 1) * mm, "end": v(-143.33, 10) * mm});
            skLineSegment(sketch, "E63.3.5.0", {"start": v(-141.6, 10) * mm, "end": v(-154.44, 1) * mm});
            skLineSegment(sketch, "E63.6.5.0", {"start": v(-143.33, 10) * mm, "end": v(-141.6, 10) * mm});
            skLineSegment(sketch, "E63.9.5.0", {"start": v(-154.44, 1) * mm, "end": v(-156.19, 1) * mm});
            skSolve(sketch);
        }
        {
            var Q0;
            Q0=makeQuery(id+"F14.imprint","IMPRINT",FACE,{"disambiguationData":[TD([[makeQuery(id+"F14.imprint","IMPRINT",EDGE,{"derivedFrom":sQuery(id+"F14.wireOp",EDGE,"E57")}),-1.0]])]});
            var Q1;
            Q1=makeQuery(id+"F14.imprint","IMPRINT",FACE,{"disambiguationData":[TD([[makeQuery(id+"F14.imprint","IMPRINT",EDGE,{"derivedFrom":sQuery(id+"F14.wireOp",EDGE,"E61.1.0.0")}),-1.0]])]});
            var Q2;
            Q2=makeQuery(id+"F14.imprint","IMPRINT",FACE,{"disambiguationData":[TD([[makeQuery(id+"F14.imprint","IMPRINT",EDGE,{"derivedFrom":sQuery(id+"F14.wireOp",EDGE,"E61.2.0.0")}),-1.0]])]});
            var Q3;
            Q3=makeQuery(id+"F14.imprint","IMPRINT",FACE,{"disambiguationData":[TD([[makeQuery(id+"F14.imprint","IMPRINT",EDGE,{"derivedFrom":sQuery(id+"F14.wireOp",EDGE,"E62.0.3.0")}),-1.0]])]});
            var Q4;
            Q4=makeQuery(id+"F14.imprint","IMPRINT",FACE,{"disambiguationData":[TD([[makeQuery(id+"F14.imprint","IMPRINT",EDGE,{"derivedFrom":sQuery(id+"F14.wireOp",EDGE,"E63.0.4.0")}),-1.0]])]});
            var Q5;
            Q5=makeQuery(id+"F14.imprint","IMPRINT",FACE,{"disambiguationData":[TD([[makeQuery(id+"F14.imprint","IMPRINT",EDGE,{"derivedFrom":sQuery(id+"F14.wireOp",EDGE,"E63.0.5.0")}),-1.0]])]});
            var Q6;
            Q6=makeQuery(id+"F13.opExtrude","SWEPT_FACE",FACE,{"disambiguationData":[OSD([sQuery(id+"F11.wireOp",EDGE,"E49")])]});
            extrude(context, id + "F15", {"entities" : qUnion([Q0, Q1, Q2, Q3, Q4, Q5]), "operationType" : NewBodyOperationType.ADD, "endBound" : BoundingType.UP_TO_SURFACE, "depth" : 25 * mm, "endBoundEntityFace" : qUnion([Q6]), "offsetDistance" : 25 * mm});
        }
    });
